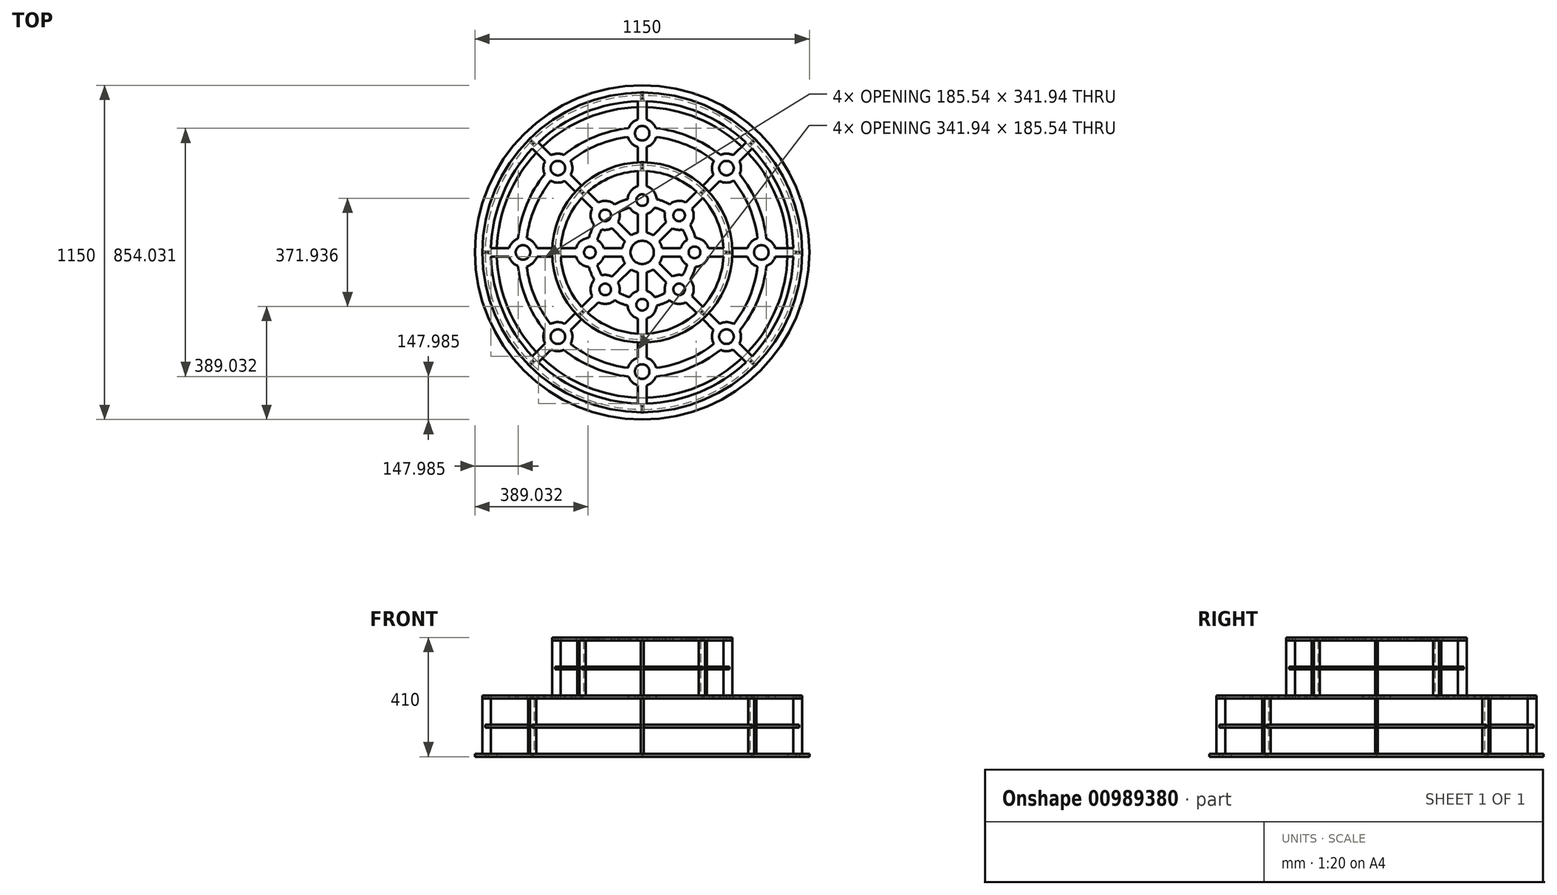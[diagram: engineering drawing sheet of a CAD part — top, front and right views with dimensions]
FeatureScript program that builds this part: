
annotation { "Feature Type Name" : "Feature", "Feature Type Description" : "" }
export const myFeature = defineFeature(function(context is Context, id is Id, definition is map)
    precondition{}
    {
        {
            var Q0;
            Q0=qCreatedBy(makeId("Top.planeOp"),FACE);
            cPlane(context, id + "F0", {"entities" : qUnion([Q0]), "cplaneType" : CPlaneType.OFFSET, "offset" : 200 * mm, "width" : 150 * mm, "height" : 150 * mm});
        }
        {
            var Q0;
            Q0=qCreatedBy(makeId("Top.planeOp"),FACE);
            cPlane(context, id + "F1", {"entities" : qUnion([Q0]), "cplaneType" : CPlaneType.OFFSET, "offset" : 200 * mm, "oppositeDirection" : true, "width" : 150 * mm, "height" : 150 * mm});
        }
        {
            var Q0;
            Q0=qCreatedBy(makeId("Top.planeOp"),FACE);
            cPlane(context, id + "F2", {"entities" : qUnion([Q0]), "cplaneType" : CPlaneType.OFFSET, "offset" : 100 * mm, "oppositeDirection" : true, "width" : 150 * mm, "height" : 150 * mm});
        }
        {
            var Q0;
            Q0=qCreatedBy(makeId("Top.planeOp"),FACE);
            cPlane(context, id + "F3", {"entities" : qUnion([Q0]), "cplaneType" : CPlaneType.OFFSET, "offset" : 100 * mm, "width" : 150 * mm, "height" : 150 * mm});
        }
        {
            var Q0;
            Q0=qCreatedBy(makeId("Top.planeOp"),FACE);
            var sketch = newSketch(context, id + "F4", { "sketchPlane" : qUnion([Q0])});
            skCircle(sketch, "E0", {"center": v(0, 0) * mm, "radius": 550 * mm});
            skArc(sketch, "E1", {"start": v(15, -519.78) * mm, "mid": v(199, -480.42) * mm, "end": v(356.94, -378.15) * mm});
            skArc(sketch, "E2", {"start": v(46.86, -427.44) * mm, "mid": v(164.55, -397.27) * mm, "end": v(269.1, -335.38) * mm});
            skArc(sketch, "E3", {"start": v(48.3, -397.07) * mm, "mid": v(153.07, -369.55) * mm, "end": v(246.62, -314.93) * mm});
            skArc(sketch, "E4", {"start": v(15, -309.64) * mm, "mid": v(118.63, -286.4) * mm, "end": v(208.34, -229.55) * mm});
            skCircle(sketch, "E5", {"center": v(0, 0) * mm, "radius": 280 * mm});
            skCircle(sketch, "E6", {"center": v(0, 0) * mm, "radius": 190 * mm, "construction": true});
            skCircle(sketch, "E7", {"center": v(0, 0) * mm, "radius": 160 * mm, "construction": true});
            skCircle(sketch, "E8", {"center": v(0, 0) * mm, "radius": 40 * mm, "construction": true});
            skCircle(sketch, "E9", {"center": v(0, 0) * mm, "radius": 70 * mm, "construction": true});
            skLineSegment(sketch, "E10", {"start": v(0, 725.48) * mm, "end": v(0, -722.46) * mm, "construction": true});
            skLineSegment(sketch, "E11", {"start": v(-695.44, 0) * mm, "end": v(901.66, 0) * mm, "construction": true});
            skArc(sketch, "E12", {"start": v(-15, -362.3) * mm, "mid": v(-36.11, -375.42) * mm, "end": v(-48.3, -397.07) * mm});
            skCircle(sketch, "E13", {"center": v(0, -410) * mm, "radius": 25 * mm});
            skLineSegment(sketch, "E14", {"start": v(15, -519.78) * mm, "end": v(15, -457.7) * mm});
            skLineSegment(sketch, "E15", {"start": v(-15, -457.7) * mm, "end": v(-15, -519.78) * mm});
            skLineSegment(sketch, "E16", {"start": v(-15, -362.3) * mm, "end": v(-15, -309.64) * mm});
            skLineSegment(sketch, "E17", {"start": v(15, -362.3) * mm, "end": v(15, -309.64) * mm});
            skArc(sketch, "E18.trimOffspring", {"start": v(-46.86, -427.44) * mm, "mid": v(-34.43, -446.26) * mm, "end": v(-15, -457.7) * mm});
            skArc(sketch, "E19.trimOffspring", {"start": v(48.3, -397.07) * mm, "mid": v(36.11, -375.42) * mm, "end": v(15, -362.3) * mm});
            skArc(sketch, "E20.trimOffspring", {"start": v(15, -457.7) * mm, "mid": v(34.43, -446.26) * mm, "end": v(46.86, -427.44) * mm});
            skArc(sketch, "E21.1.0", {"start": v(334.25, -313.03) * mm, "mid": v(339.9, -291.2) * mm, "end": v(335.38, -269.1) * mm});
            skCircle(sketch, "E21.1.1", {"center": v(289.91, -289.91) * mm, "radius": 25 * mm});
            skLineSegment(sketch, "E21.1.2", {"start": v(266.8, -245.58) * mm, "end": v(229.55, -208.34) * mm});
            skLineSegment(sketch, "E21.1.3", {"start": v(245.58, -266.8) * mm, "end": v(208.34, -229.55) * mm});
            skArc(sketch, "E21.1.4", {"start": v(245.58, -266.8) * mm, "mid": v(239.93, -291) * mm, "end": v(246.62, -314.93) * mm});
            skArc(sketch, "E21.1.5", {"start": v(269.1, -335.38) * mm, "mid": v(291.2, -339.9) * mm, "end": v(313.03, -334.25) * mm});
            skArc(sketch, "E21.1.6", {"start": v(314.93, -246.62) * mm, "mid": v(291, -239.93) * mm, "end": v(266.8, -245.58) * mm});
            skLineSegment(sketch, "E21.1.7", {"start": v(378.15, -356.94) * mm, "end": v(334.25, -313.03) * mm});
            skLineSegment(sketch, "E21.1.8", {"start": v(313.03, -334.25) * mm, "end": v(356.94, -378.15) * mm});
            skArc(sketch, "E21.2.0", {"start": v(457.7, 15) * mm, "mid": v(446.26, 34.43) * mm, "end": v(427.44, 46.86) * mm});
            skCircle(sketch, "E21.2.1", {"center": v(410, 0) * mm, "radius": 25 * mm});
            skLineSegment(sketch, "E21.2.2", {"start": v(362.3, 15) * mm, "end": v(309.64, 15) * mm});
            skLineSegment(sketch, "E21.2.3", {"start": v(362.3, -15) * mm, "end": v(309.64, -15) * mm});
            skArc(sketch, "E21.2.4", {"start": v(362.3, -15) * mm, "mid": v(375.42, -36.11) * mm, "end": v(397.07, -48.3) * mm});
            skArc(sketch, "E21.2.5", {"start": v(427.44, -46.86) * mm, "mid": v(446.26, -34.43) * mm, "end": v(457.7, -15) * mm});
            skArc(sketch, "E21.2.6", {"start": v(397.07, 48.3) * mm, "mid": v(375.42, 36.11) * mm, "end": v(362.3, 15) * mm});
            skLineSegment(sketch, "E21.2.7", {"start": v(519.78, 15) * mm, "end": v(457.7, 15) * mm});
            skLineSegment(sketch, "E21.2.8", {"start": v(457.7, -15) * mm, "end": v(519.78, -15) * mm});
            skArc(sketch, "E21.3.0", {"start": v(313.03, 334.25) * mm, "mid": v(291.2, 339.9) * mm, "end": v(269.1, 335.38) * mm});
            skCircle(sketch, "E21.3.1", {"center": v(289.91, 289.91) * mm, "radius": 25 * mm});
            skLineSegment(sketch, "E21.3.2", {"start": v(245.58, 266.8) * mm, "end": v(208.34, 229.55) * mm});
            skLineSegment(sketch, "E21.3.3", {"start": v(266.8, 245.58) * mm, "end": v(229.55, 208.34) * mm});
            skArc(sketch, "E21.3.4", {"start": v(266.8, 245.58) * mm, "mid": v(291, 239.93) * mm, "end": v(314.93, 246.62) * mm});
            skArc(sketch, "E21.3.5", {"start": v(335.38, 269.1) * mm, "mid": v(339.9, 291.2) * mm, "end": v(334.25, 313.03) * mm});
            skArc(sketch, "E21.3.6", {"start": v(246.62, 314.93) * mm, "mid": v(239.93, 291) * mm, "end": v(245.58, 266.8) * mm});
            skLineSegment(sketch, "E21.3.7", {"start": v(356.94, 378.15) * mm, "end": v(313.03, 334.25) * mm});
            skLineSegment(sketch, "E21.3.8", {"start": v(334.25, 313.03) * mm, "end": v(378.15, 356.94) * mm});
            skArc(sketch, "E21.4.0", {"start": v(-15, 457.7) * mm, "mid": v(-34.43, 446.26) * mm, "end": v(-46.86, 427.44) * mm});
            skCircle(sketch, "E21.4.1", {"center": v(0, 410) * mm, "radius": 25 * mm});
            skLineSegment(sketch, "E21.4.2", {"start": v(-15, 362.3) * mm, "end": v(-15, 309.64) * mm});
            skLineSegment(sketch, "E21.4.3", {"start": v(15, 362.3) * mm, "end": v(15, 309.64) * mm});
            skArc(sketch, "E21.4.4", {"start": v(15, 362.3) * mm, "mid": v(36.11, 375.42) * mm, "end": v(48.3, 397.07) * mm});
            skArc(sketch, "E21.4.5", {"start": v(46.86, 427.44) * mm, "mid": v(34.43, 446.26) * mm, "end": v(15, 457.7) * mm});
            skArc(sketch, "E21.4.6", {"start": v(-48.3, 397.07) * mm, "mid": v(-36.11, 375.42) * mm, "end": v(-15, 362.3) * mm});
            skLineSegment(sketch, "E21.4.7", {"start": v(-15, 519.78) * mm, "end": v(-15, 457.7) * mm});
            skLineSegment(sketch, "E21.4.8", {"start": v(15, 457.7) * mm, "end": v(15, 519.78) * mm});
            skArc(sketch, "E21.5.0", {"start": v(-334.25, 313.03) * mm, "mid": v(-339.9, 291.2) * mm, "end": v(-335.38, 269.1) * mm});
            skCircle(sketch, "E21.5.1", {"center": v(-289.91, 289.91) * mm, "radius": 25 * mm});
            skLineSegment(sketch, "E21.5.2", {"start": v(-266.8, 245.58) * mm, "end": v(-229.55, 208.34) * mm});
            skLineSegment(sketch, "E21.5.3", {"start": v(-245.58, 266.8) * mm, "end": v(-208.34, 229.55) * mm});
            skArc(sketch, "E21.5.4", {"start": v(-245.58, 266.8) * mm, "mid": v(-239.93, 291) * mm, "end": v(-246.62, 314.93) * mm});
            skArc(sketch, "E21.5.5", {"start": v(-269.1, 335.38) * mm, "mid": v(-291.2, 339.9) * mm, "end": v(-313.03, 334.25) * mm});
            skArc(sketch, "E21.5.6", {"start": v(-314.93, 246.62) * mm, "mid": v(-291, 239.93) * mm, "end": v(-266.8, 245.58) * mm});
            skLineSegment(sketch, "E21.5.7", {"start": v(-378.15, 356.94) * mm, "end": v(-334.25, 313.03) * mm});
            skLineSegment(sketch, "E21.5.8", {"start": v(-313.03, 334.25) * mm, "end": v(-356.94, 378.15) * mm});
            skArc(sketch, "E21.6.0", {"start": v(-457.7, -15) * mm, "mid": v(-446.26, -34.43) * mm, "end": v(-427.44, -46.86) * mm});
            skCircle(sketch, "E21.6.1", {"center": v(-410, 0) * mm, "radius": 25 * mm});
            skLineSegment(sketch, "E21.6.2", {"start": v(-362.3, -15) * mm, "end": v(-309.64, -15) * mm});
            skLineSegment(sketch, "E21.6.3", {"start": v(-362.3, 15) * mm, "end": v(-309.64, 15) * mm});
            skArc(sketch, "E21.6.4", {"start": v(-362.3, 15) * mm, "mid": v(-375.42, 36.11) * mm, "end": v(-397.07, 48.3) * mm});
            skArc(sketch, "E21.6.5", {"start": v(-427.44, 46.86) * mm, "mid": v(-446.26, 34.43) * mm, "end": v(-457.7, 15) * mm});
            skArc(sketch, "E21.6.6", {"start": v(-397.07, -48.3) * mm, "mid": v(-375.42, -36.11) * mm, "end": v(-362.3, -15) * mm});
            skLineSegment(sketch, "E21.6.7", {"start": v(-519.78, -15) * mm, "end": v(-457.7, -15) * mm});
            skLineSegment(sketch, "E21.6.8", {"start": v(-457.7, 15) * mm, "end": v(-519.78, 15) * mm});
            skArc(sketch, "E21.7.0", {"start": v(-313.03, -334.25) * mm, "mid": v(-291.2, -339.9) * mm, "end": v(-269.1, -335.38) * mm});
            skCircle(sketch, "E21.7.1", {"center": v(-289.91, -289.91) * mm, "radius": 25 * mm});
            skLineSegment(sketch, "E21.7.2", {"start": v(-245.58, -266.8) * mm, "end": v(-208.34, -229.55) * mm});
            skLineSegment(sketch, "E21.7.3", {"start": v(-266.8, -245.58) * mm, "end": v(-229.55, -208.34) * mm});
            skArc(sketch, "E21.7.4", {"start": v(-266.8, -245.58) * mm, "mid": v(-291, -239.93) * mm, "end": v(-314.93, -246.62) * mm});
            skArc(sketch, "E21.7.5", {"start": v(-335.38, -269.1) * mm, "mid": v(-339.9, -291.2) * mm, "end": v(-334.25, -313.03) * mm});
            skArc(sketch, "E21.7.6", {"start": v(-246.62, -314.93) * mm, "mid": v(-239.93, -291) * mm, "end": v(-245.58, -266.8) * mm});
            skLineSegment(sketch, "E21.7.7", {"start": v(-356.94, -378.15) * mm, "end": v(-313.03, -334.25) * mm});
            skLineSegment(sketch, "E21.7.8", {"start": v(-334.25, -313.03) * mm, "end": v(-378.15, -356.94) * mm});
            skArc(sketch, "E22.trimOffspring", {"start": v(-246.62, -314.93) * mm, "mid": v(-153.07, -369.55) * mm, "end": v(-48.3, -397.07) * mm});
            skArc(sketch, "E23.trimOffspring", {"start": v(-269.1, -335.38) * mm, "mid": v(-164.55, -397.27) * mm, "end": v(-46.86, -427.44) * mm});
            skArc(sketch, "E24.trimOffspring", {"start": v(-356.94, -378.15) * mm, "mid": v(-199, -480.42) * mm, "end": v(-15, -519.78) * mm});
            skArc(sketch, "E25.trimOffspring", {"start": v(-208.34, -229.55) * mm, "mid": v(-118.63, -286.4) * mm, "end": v(-15, -309.64) * mm});
            skArc(sketch, "E26.trimOffspring", {"start": v(-397.07, -48.3) * mm, "mid": v(-369.55, -153.07) * mm, "end": v(-314.93, -246.62) * mm});
            skArc(sketch, "E27.trimOffspring", {"start": v(-427.44, -46.86) * mm, "mid": v(-397.27, -164.55) * mm, "end": v(-335.38, -269.1) * mm});
            skArc(sketch, "E28.trimOffspring", {"start": v(-309.64, -15) * mm, "mid": v(-286.4, -118.63) * mm, "end": v(-229.55, -208.34) * mm});
            skArc(sketch, "E29.trimOffspring", {"start": v(-519.78, -15) * mm, "mid": v(-480.42, -199) * mm, "end": v(-378.15, -356.94) * mm});
            skArc(sketch, "E30.trimOffspring", {"start": v(-314.93, 246.62) * mm, "mid": v(-369.55, 153.07) * mm, "end": v(-397.07, 48.3) * mm});
            skArc(sketch, "E31.trimOffspring", {"start": v(-335.38, 269.1) * mm, "mid": v(-397.27, 164.55) * mm, "end": v(-427.44, 46.86) * mm});
            skArc(sketch, "E32.trimOffspring", {"start": v(-378.15, 356.94) * mm, "mid": v(-480.42, 199) * mm, "end": v(-519.78, 15) * mm});
            skArc(sketch, "E33.trimOffspring", {"start": v(-229.55, 208.34) * mm, "mid": v(-286.4, 118.63) * mm, "end": v(-309.64, 15) * mm});
            skArc(sketch, "E34.trimOffspring", {"start": v(-15, 309.64) * mm, "mid": v(-118.63, 286.4) * mm, "end": v(-208.34, 229.55) * mm});
            skArc(sketch, "E35.trimOffspring", {"start": v(-48.3, 397.07) * mm, "mid": v(-153.07, 369.55) * mm, "end": v(-246.62, 314.93) * mm});
            skArc(sketch, "E36.trimOffspring", {"start": v(-46.86, 427.44) * mm, "mid": v(-164.55, 397.27) * mm, "end": v(-269.1, 335.38) * mm});
            skArc(sketch, "E37.trimOffspring", {"start": v(-15, 519.78) * mm, "mid": v(-199, 480.42) * mm, "end": v(-356.94, 378.15) * mm});
            skArc(sketch, "E38.trimOffspring", {"start": v(269.1, 335.38) * mm, "mid": v(164.55, 397.27) * mm, "end": v(46.86, 427.44) * mm});
            skArc(sketch, "E39.trimOffspring", {"start": v(246.62, 314.93) * mm, "mid": v(153.07, 369.55) * mm, "end": v(48.3, 397.07) * mm});
            skArc(sketch, "E40.trimOffspring", {"start": v(208.34, 229.55) * mm, "mid": v(118.63, 286.4) * mm, "end": v(15, 309.64) * mm});
            skArc(sketch, "E41.trimOffspring", {"start": v(356.94, 378.15) * mm, "mid": v(199, 480.42) * mm, "end": v(15, 519.78) * mm});
            skArc(sketch, "E42.trimOffspring", {"start": v(309.64, 15) * mm, "mid": v(286.4, 118.63) * mm, "end": v(229.55, 208.34) * mm});
            skArc(sketch, "E43.trimOffspring", {"start": v(397.07, 48.3) * mm, "mid": v(369.55, 153.07) * mm, "end": v(314.93, 246.62) * mm});
            skArc(sketch, "E44.trimOffspring", {"start": v(427.44, 46.86) * mm, "mid": v(397.27, 164.55) * mm, "end": v(335.38, 269.1) * mm});
            skArc(sketch, "E45.trimOffspring", {"start": v(519.78, 15) * mm, "mid": v(480.42, 199) * mm, "end": v(378.15, 356.94) * mm});
            skArc(sketch, "E46.trimOffspring", {"start": v(335.38, -269.1) * mm, "mid": v(397.27, -164.55) * mm, "end": v(427.44, -46.86) * mm});
            skArc(sketch, "E47.trimOffspring", {"start": v(314.93, -246.62) * mm, "mid": v(369.55, -153.07) * mm, "end": v(397.07, -48.3) * mm});
            skArc(sketch, "E48.trimOffspring", {"start": v(378.15, -356.94) * mm, "mid": v(480.42, -199) * mm, "end": v(519.78, -15) * mm});
            skArc(sketch, "E49.trimOffspring", {"start": v(229.55, -208.34) * mm, "mid": v(286.4, -118.63) * mm, "end": v(309.64, -15) * mm});
            skLineSegment(sketch, "E50.bottom", {"start": v(4.9, 530) * mm, "end": v(1, 530) * mm});
            skLineSegment(sketch, "E50.top", {"start": v(4.9, 540) * mm, "end": v(1, 540) * mm});
            skLineSegment(sketch, "E50.left", {"start": v(4.9, 530) * mm, "end": v(4.9, 540) * mm});
            skLineSegment(sketch, "E50.right", {"start": v(-4.9, 530) * mm, "end": v(-4.9, 540) * mm});
            skPoint(sketch, "E50.middle", {"position": v(0, 535) * mm});
            skLineSegment(sketch, "E51", {"start": v(0, 541) * mm, "end": v(-1, 540) * mm});
            skLineSegment(sketch, "E52", {"start": v(0, 541) * mm, "end": v(1, 540) * mm});
            skLineSegment(sketch, "E53.trimOffspring", {"start": v(-1, 540) * mm, "end": v(-4.9, 540) * mm});
            skLineSegment(sketch, "E54", {"start": v(0, 529) * mm, "end": v(-1, 530) * mm});
            skLineSegment(sketch, "E55", {"start": v(0, 529) * mm, "end": v(1, 530) * mm});
            skLineSegment(sketch, "E56.trimOffspring", {"start": v(-1, 530) * mm, "end": v(-4.9, 530) * mm});
            skPoint(sketch, "E57.1.0", {"position": v(-378.3, 378.3) * mm});
            skLineSegment(sketch, "E57.1.1", {"start": v(-378.23, 371.3) * mm, "end": v(-385.3, 378.37) * mm});
            skLineSegment(sketch, "E57.1.2", {"start": v(-371.3, 378.23) * mm, "end": v(-378.37, 385.3) * mm});
            skLineSegment(sketch, "E57.1.3", {"start": v(-371.3, 378.23) * mm, "end": v(-374.06, 375.47) * mm});
            skLineSegment(sketch, "E57.1.4", {"start": v(-374.06, 374.06) * mm, "end": v(-374.06, 375.47) * mm});
            skLineSegment(sketch, "E57.1.5", {"start": v(-374.06, 374.06) * mm, "end": v(-375.47, 374.06) * mm});
            skLineSegment(sketch, "E57.1.6", {"start": v(-375.47, 374.06) * mm, "end": v(-378.23, 371.3) * mm});
            skLineSegment(sketch, "E57.1.7", {"start": v(-378.37, 385.3) * mm, "end": v(-381.13, 382.54) * mm});
            skLineSegment(sketch, "E57.1.8", {"start": v(-382.54, 381.13) * mm, "end": v(-385.3, 378.37) * mm});
            skLineSegment(sketch, "E57.1.9", {"start": v(-382.54, 382.54) * mm, "end": v(-381.13, 382.54) * mm});
            skLineSegment(sketch, "E57.1.10", {"start": v(-382.54, 382.54) * mm, "end": v(-382.54, 381.13) * mm});
            skPoint(sketch, "E57.2.0", {"position": v(-535, 0) * mm});
            skLineSegment(sketch, "E57.2.1", {"start": v(-530, -4.9) * mm, "end": v(-540, -4.9) * mm});
            skLineSegment(sketch, "E57.2.2", {"start": v(-530, 4.9) * mm, "end": v(-540, 4.9) * mm});
            skLineSegment(sketch, "E57.2.3", {"start": v(-530, 4.9) * mm, "end": v(-530, 1) * mm});
            skLineSegment(sketch, "E57.2.4", {"start": v(-529, 0) * mm, "end": v(-530, 1) * mm});
            skLineSegment(sketch, "E57.2.5", {"start": v(-529, 0) * mm, "end": v(-530, -1) * mm});
            skLineSegment(sketch, "E57.2.6", {"start": v(-530, -1) * mm, "end": v(-530, -4.9) * mm});
            skLineSegment(sketch, "E57.2.7", {"start": v(-540, 4.9) * mm, "end": v(-540, 1) * mm});
            skLineSegment(sketch, "E57.2.8", {"start": v(-540, -1) * mm, "end": v(-540, -4.9) * mm});
            skLineSegment(sketch, "E57.2.9", {"start": v(-541, 0) * mm, "end": v(-540, 1) * mm});
            skLineSegment(sketch, "E57.2.10", {"start": v(-541, 0) * mm, "end": v(-540, -1) * mm});
            skPoint(sketch, "E57.3.0", {"position": v(-378.3, -378.3) * mm});
            skLineSegment(sketch, "E57.3.1", {"start": v(-371.3, -378.23) * mm, "end": v(-378.37, -385.3) * mm});
            skLineSegment(sketch, "E57.3.2", {"start": v(-378.23, -371.3) * mm, "end": v(-385.3, -378.37) * mm});
            skLineSegment(sketch, "E57.3.3", {"start": v(-378.23, -371.3) * mm, "end": v(-375.47, -374.06) * mm});
            skLineSegment(sketch, "E57.3.4", {"start": v(-374.06, -374.06) * mm, "end": v(-375.47, -374.06) * mm});
            skLineSegment(sketch, "E57.3.5", {"start": v(-374.06, -374.06) * mm, "end": v(-374.06, -375.47) * mm});
            skLineSegment(sketch, "E57.3.6", {"start": v(-374.06, -375.47) * mm, "end": v(-371.3, -378.23) * mm});
            skLineSegment(sketch, "E57.3.7", {"start": v(-385.3, -378.37) * mm, "end": v(-382.54, -381.13) * mm});
            skLineSegment(sketch, "E57.3.8", {"start": v(-381.13, -382.54) * mm, "end": v(-378.37, -385.3) * mm});
            skLineSegment(sketch, "E57.3.9", {"start": v(-382.54, -382.54) * mm, "end": v(-382.54, -381.13) * mm});
            skLineSegment(sketch, "E57.3.10", {"start": v(-382.54, -382.54) * mm, "end": v(-381.13, -382.54) * mm});
            skPoint(sketch, "E57.4.0", {"position": v(0, -535) * mm});
            skLineSegment(sketch, "E57.4.1", {"start": v(4.9, -530) * mm, "end": v(4.9, -540) * mm});
            skLineSegment(sketch, "E57.4.2", {"start": v(-4.9, -530) * mm, "end": v(-4.9, -540) * mm});
            skLineSegment(sketch, "E57.4.3", {"start": v(-4.9, -530) * mm, "end": v(-1, -530) * mm});
            skLineSegment(sketch, "E57.4.4", {"start": v(0, -529) * mm, "end": v(-1, -530) * mm});
            skLineSegment(sketch, "E57.4.5", {"start": v(0, -529) * mm, "end": v(1, -530) * mm});
            skLineSegment(sketch, "E57.4.6", {"start": v(1, -530) * mm, "end": v(4.9, -530) * mm});
            skLineSegment(sketch, "E57.4.7", {"start": v(-4.9, -540) * mm, "end": v(-1, -540) * mm});
            skLineSegment(sketch, "E57.4.8", {"start": v(1, -540) * mm, "end": v(4.9, -540) * mm});
            skLineSegment(sketch, "E57.4.9", {"start": v(0, -541) * mm, "end": v(-1, -540) * mm});
            skLineSegment(sketch, "E57.4.10", {"start": v(0, -541) * mm, "end": v(1, -540) * mm});
            skPoint(sketch, "E57.5.0", {"position": v(378.3, -378.3) * mm});
            skLineSegment(sketch, "E57.5.1", {"start": v(378.23, -371.3) * mm, "end": v(385.3, -378.37) * mm});
            skLineSegment(sketch, "E57.5.2", {"start": v(371.3, -378.23) * mm, "end": v(378.37, -385.3) * mm});
            skLineSegment(sketch, "E57.5.3", {"start": v(371.3, -378.23) * mm, "end": v(374.06, -375.47) * mm});
            skLineSegment(sketch, "E57.5.4", {"start": v(374.06, -374.06) * mm, "end": v(374.06, -375.47) * mm});
            skLineSegment(sketch, "E57.5.5", {"start": v(374.06, -374.06) * mm, "end": v(375.47, -374.06) * mm});
            skLineSegment(sketch, "E57.5.6", {"start": v(375.47, -374.06) * mm, "end": v(378.23, -371.3) * mm});
            skLineSegment(sketch, "E57.5.7", {"start": v(378.37, -385.3) * mm, "end": v(381.13, -382.54) * mm});
            skLineSegment(sketch, "E57.5.8", {"start": v(382.54, -381.13) * mm, "end": v(385.3, -378.37) * mm});
            skLineSegment(sketch, "E57.5.9", {"start": v(382.54, -382.54) * mm, "end": v(381.13, -382.54) * mm});
            skLineSegment(sketch, "E57.5.10", {"start": v(382.54, -382.54) * mm, "end": v(382.54, -381.13) * mm});
            skPoint(sketch, "E57.6.0", {"position": v(535, 0) * mm});
            skLineSegment(sketch, "E57.6.1", {"start": v(530, 4.9) * mm, "end": v(540, 4.9) * mm});
            skLineSegment(sketch, "E57.6.2", {"start": v(530, -4.9) * mm, "end": v(540, -4.9) * mm});
            skLineSegment(sketch, "E57.6.3", {"start": v(530, -4.9) * mm, "end": v(530, -1) * mm});
            skLineSegment(sketch, "E57.6.4", {"start": v(529, 0) * mm, "end": v(530, -1) * mm});
            skLineSegment(sketch, "E57.6.5", {"start": v(529, 0) * mm, "end": v(530, 1) * mm});
            skLineSegment(sketch, "E57.6.6", {"start": v(530, 1) * mm, "end": v(530, 4.9) * mm});
            skLineSegment(sketch, "E57.6.7", {"start": v(540, -4.9) * mm, "end": v(540, -1) * mm});
            skLineSegment(sketch, "E57.6.8", {"start": v(540, 1) * mm, "end": v(540, 4.9) * mm});
            skLineSegment(sketch, "E57.6.9", {"start": v(541, 0) * mm, "end": v(540, -1) * mm});
            skLineSegment(sketch, "E57.6.10", {"start": v(541, 0) * mm, "end": v(540, 1) * mm});
            skPoint(sketch, "E57.7.0", {"position": v(378.3, 378.3) * mm});
            skLineSegment(sketch, "E57.7.1", {"start": v(371.3, 378.23) * mm, "end": v(378.37, 385.3) * mm});
            skLineSegment(sketch, "E57.7.2", {"start": v(378.23, 371.3) * mm, "end": v(385.3, 378.37) * mm});
            skLineSegment(sketch, "E57.7.3", {"start": v(378.23, 371.3) * mm, "end": v(375.47, 374.06) * mm});
            skLineSegment(sketch, "E57.7.4", {"start": v(374.06, 374.06) * mm, "end": v(375.47, 374.06) * mm});
            skLineSegment(sketch, "E57.7.5", {"start": v(374.06, 374.06) * mm, "end": v(374.06, 375.47) * mm});
            skLineSegment(sketch, "E57.7.6", {"start": v(374.06, 375.47) * mm, "end": v(371.3, 378.23) * mm});
            skLineSegment(sketch, "E57.7.7", {"start": v(385.3, 378.37) * mm, "end": v(382.54, 381.13) * mm});
            skLineSegment(sketch, "E57.7.8", {"start": v(381.13, 382.54) * mm, "end": v(378.37, 385.3) * mm});
            skLineSegment(sketch, "E57.7.9", {"start": v(382.54, 382.54) * mm, "end": v(382.54, 381.13) * mm});
            skLineSegment(sketch, "E57.7.10", {"start": v(382.54, 382.54) * mm, "end": v(381.13, 382.54) * mm});
            skLineSegment(sketch, "E58.bottom", {"start": v(4.9, 290) * mm, "end": v(1, 290) * mm});
            skLineSegment(sketch, "E58.top", {"start": v(4.9, 300) * mm, "end": v(1, 300) * mm});
            skLineSegment(sketch, "E58.left", {"start": v(4.9, 290) * mm, "end": v(4.9, 300) * mm});
            skLineSegment(sketch, "E58.right", {"start": v(-4.9, 290) * mm, "end": v(-4.9, 300) * mm});
            skPoint(sketch, "E58.middle", {"position": v(0, 295) * mm});
            skLineSegment(sketch, "E59", {"start": v(0, 301) * mm, "end": v(-1, 300) * mm});
            skLineSegment(sketch, "E60", {"start": v(0, 301) * mm, "end": v(1, 300) * mm});
            skLineSegment(sketch, "E61.trimOffspring", {"start": v(-1, 300) * mm, "end": v(-4.9, 300) * mm});
            skLineSegment(sketch, "E62", {"start": v(0, 289) * mm, "end": v(-1, 290) * mm});
            skLineSegment(sketch, "E63", {"start": v(0, 289) * mm, "end": v(1, 290) * mm});
            skLineSegment(sketch, "E64.trimOffspring", {"start": v(-1, 290) * mm, "end": v(-4.9, 290) * mm});
            skLineSegment(sketch, "E65.1.0", {"start": v(-201.6, 208.53) * mm, "end": v(-208.67, 215.6) * mm});
            skPoint(sketch, "E65.1.1", {"position": v(-208.6, 208.6) * mm});
            skLineSegment(sketch, "E65.1.2", {"start": v(-208.53, 201.6) * mm, "end": v(-215.6, 208.67) * mm});
            skLineSegment(sketch, "E65.1.3", {"start": v(-205.77, 204.35) * mm, "end": v(-208.53, 201.6) * mm});
            skLineSegment(sketch, "E65.1.4", {"start": v(-208.67, 215.6) * mm, "end": v(-211.42, 212.84) * mm});
            skLineSegment(sketch, "E65.1.5", {"start": v(-201.6, 208.53) * mm, "end": v(-204.35, 205.77) * mm});
            skLineSegment(sketch, "E65.1.6", {"start": v(-212.84, 211.42) * mm, "end": v(-215.6, 208.67) * mm});
            skLineSegment(sketch, "E65.1.7", {"start": v(-204.35, 204.35) * mm, "end": v(-205.77, 204.35) * mm});
            skLineSegment(sketch, "E65.1.8", {"start": v(-212.84, 212.84) * mm, "end": v(-211.42, 212.84) * mm});
            skLineSegment(sketch, "E65.1.9", {"start": v(-212.84, 212.84) * mm, "end": v(-212.84, 211.42) * mm});
            skLineSegment(sketch, "E65.1.10", {"start": v(-204.35, 204.35) * mm, "end": v(-204.35, 205.77) * mm});
            skLineSegment(sketch, "E65.2.0", {"start": v(-290, 4.9) * mm, "end": v(-300, 4.9) * mm});
            skPoint(sketch, "E65.2.1", {"position": v(-295, 0) * mm});
            skLineSegment(sketch, "E65.2.2", {"start": v(-290, -4.9) * mm, "end": v(-300, -4.9) * mm});
            skLineSegment(sketch, "E65.2.3", {"start": v(-290, -1) * mm, "end": v(-290, -4.9) * mm});
            skLineSegment(sketch, "E65.2.4", {"start": v(-300, 4.9) * mm, "end": v(-300, 1) * mm});
            skLineSegment(sketch, "E65.2.5", {"start": v(-290, 4.9) * mm, "end": v(-290, 1) * mm});
            skLineSegment(sketch, "E65.2.6", {"start": v(-300, -1) * mm, "end": v(-300, -4.9) * mm});
            skLineSegment(sketch, "E65.2.7", {"start": v(-289, 0) * mm, "end": v(-290, -1) * mm});
            skLineSegment(sketch, "E65.2.8", {"start": v(-301, 0) * mm, "end": v(-300, 1) * mm});
            skLineSegment(sketch, "E65.2.9", {"start": v(-301, 0) * mm, "end": v(-300, -1) * mm});
            skLineSegment(sketch, "E65.2.10", {"start": v(-289, 0) * mm, "end": v(-290, 1) * mm});
            skLineSegment(sketch, "E65.3.0", {"start": v(-208.53, -201.6) * mm, "end": v(-215.6, -208.67) * mm});
            skPoint(sketch, "E65.3.1", {"position": v(-208.6, -208.6) * mm});
            skLineSegment(sketch, "E65.3.2", {"start": v(-201.6, -208.53) * mm, "end": v(-208.67, -215.6) * mm});
            skLineSegment(sketch, "E65.3.3", {"start": v(-204.35, -205.77) * mm, "end": v(-201.6, -208.53) * mm});
            skLineSegment(sketch, "E65.3.4", {"start": v(-215.6, -208.67) * mm, "end": v(-212.84, -211.42) * mm});
            skLineSegment(sketch, "E65.3.5", {"start": v(-208.53, -201.6) * mm, "end": v(-205.77, -204.35) * mm});
            skLineSegment(sketch, "E65.3.6", {"start": v(-211.42, -212.84) * mm, "end": v(-208.67, -215.6) * mm});
            skLineSegment(sketch, "E65.3.7", {"start": v(-204.35, -204.35) * mm, "end": v(-204.35, -205.77) * mm});
            skLineSegment(sketch, "E65.3.8", {"start": v(-212.84, -212.84) * mm, "end": v(-212.84, -211.42) * mm});
            skLineSegment(sketch, "E65.3.9", {"start": v(-212.84, -212.84) * mm, "end": v(-211.42, -212.84) * mm});
            skLineSegment(sketch, "E65.3.10", {"start": v(-204.35, -204.35) * mm, "end": v(-205.77, -204.35) * mm});
            skLineSegment(sketch, "E65.4.0", {"start": v(-4.9, -290) * mm, "end": v(-4.9, -300) * mm});
            skPoint(sketch, "E65.4.1", {"position": v(0, -295) * mm});
            skLineSegment(sketch, "E65.4.2", {"start": v(4.9, -290) * mm, "end": v(4.9, -300) * mm});
            skLineSegment(sketch, "E65.4.3", {"start": v(1, -290) * mm, "end": v(4.9, -290) * mm});
            skLineSegment(sketch, "E65.4.4", {"start": v(-4.9, -300) * mm, "end": v(-1, -300) * mm});
            skLineSegment(sketch, "E65.4.5", {"start": v(-4.9, -290) * mm, "end": v(-1, -290) * mm});
            skLineSegment(sketch, "E65.4.6", {"start": v(1, -300) * mm, "end": v(4.9, -300) * mm});
            skLineSegment(sketch, "E65.4.7", {"start": v(0, -289) * mm, "end": v(1, -290) * mm});
            skLineSegment(sketch, "E65.4.8", {"start": v(0, -301) * mm, "end": v(-1, -300) * mm});
            skLineSegment(sketch, "E65.4.9", {"start": v(0, -301) * mm, "end": v(1, -300) * mm});
            skLineSegment(sketch, "E65.4.10", {"start": v(0, -289) * mm, "end": v(-1, -290) * mm});
            skLineSegment(sketch, "E65.5.0", {"start": v(201.6, -208.53) * mm, "end": v(208.67, -215.6) * mm});
            skPoint(sketch, "E65.5.1", {"position": v(208.6, -208.6) * mm});
            skLineSegment(sketch, "E65.5.2", {"start": v(208.53, -201.6) * mm, "end": v(215.6, -208.67) * mm});
            skLineSegment(sketch, "E65.5.3", {"start": v(205.77, -204.35) * mm, "end": v(208.53, -201.6) * mm});
            skLineSegment(sketch, "E65.5.4", {"start": v(208.67, -215.6) * mm, "end": v(211.42, -212.84) * mm});
            skLineSegment(sketch, "E65.5.5", {"start": v(201.6, -208.53) * mm, "end": v(204.35, -205.77) * mm});
            skLineSegment(sketch, "E65.5.6", {"start": v(212.84, -211.42) * mm, "end": v(215.6, -208.67) * mm});
            skLineSegment(sketch, "E65.5.7", {"start": v(204.35, -204.35) * mm, "end": v(205.77, -204.35) * mm});
            skLineSegment(sketch, "E65.5.8", {"start": v(212.84, -212.84) * mm, "end": v(211.42, -212.84) * mm});
            skLineSegment(sketch, "E65.5.9", {"start": v(212.84, -212.84) * mm, "end": v(212.84, -211.42) * mm});
            skLineSegment(sketch, "E65.5.10", {"start": v(204.35, -204.35) * mm, "end": v(204.35, -205.77) * mm});
            skLineSegment(sketch, "E65.6.0", {"start": v(290, -4.9) * mm, "end": v(300, -4.9) * mm});
            skPoint(sketch, "E65.6.1", {"position": v(295, 0) * mm});
            skLineSegment(sketch, "E65.6.2", {"start": v(290, 4.9) * mm, "end": v(300, 4.9) * mm});
            skLineSegment(sketch, "E65.6.3", {"start": v(290, 1) * mm, "end": v(290, 4.9) * mm});
            skLineSegment(sketch, "E65.6.4", {"start": v(300, -4.9) * mm, "end": v(300, -1) * mm});
            skLineSegment(sketch, "E65.6.5", {"start": v(290, -4.9) * mm, "end": v(290, -1) * mm});
            skLineSegment(sketch, "E65.6.6", {"start": v(300, 1) * mm, "end": v(300, 4.9) * mm});
            skLineSegment(sketch, "E65.6.7", {"start": v(289, 0) * mm, "end": v(290, 1) * mm});
            skLineSegment(sketch, "E65.6.8", {"start": v(301, 0) * mm, "end": v(300, -1) * mm});
            skLineSegment(sketch, "E65.6.9", {"start": v(301, 0) * mm, "end": v(300, 1) * mm});
            skLineSegment(sketch, "E65.6.10", {"start": v(289, 0) * mm, "end": v(290, -1) * mm});
            skLineSegment(sketch, "E65.7.0", {"start": v(208.53, 201.6) * mm, "end": v(215.6, 208.67) * mm});
            skPoint(sketch, "E65.7.1", {"position": v(208.6, 208.6) * mm});
            skLineSegment(sketch, "E65.7.2", {"start": v(201.6, 208.53) * mm, "end": v(208.67, 215.6) * mm});
            skLineSegment(sketch, "E65.7.3", {"start": v(204.35, 205.77) * mm, "end": v(201.6, 208.53) * mm});
            skLineSegment(sketch, "E65.7.4", {"start": v(215.6, 208.67) * mm, "end": v(212.84, 211.42) * mm});
            skLineSegment(sketch, "E65.7.5", {"start": v(208.53, 201.6) * mm, "end": v(205.77, 204.35) * mm});
            skLineSegment(sketch, "E65.7.6", {"start": v(211.42, 212.84) * mm, "end": v(208.67, 215.6) * mm});
            skLineSegment(sketch, "E65.7.7", {"start": v(204.35, 204.35) * mm, "end": v(204.35, 205.77) * mm});
            skLineSegment(sketch, "E65.7.8", {"start": v(212.84, 212.84) * mm, "end": v(212.84, 211.42) * mm});
            skLineSegment(sketch, "E65.7.9", {"start": v(212.84, 212.84) * mm, "end": v(211.42, 212.84) * mm});
            skLineSegment(sketch, "E65.7.10", {"start": v(204.35, 204.35) * mm, "end": v(205.77, 204.35) * mm});
            skSolve(sketch);
        }
        {
            var Q0;
            Q0=qSketchRegion(id+"F4",true);
            extrude(context, id + "F5", {"entities" : qUnion([Q0]), "depth" : 10 * mm, "offsetDistance" : 25 * mm});
        }
        {
            var Q0;
            Q0=qCreatedBy(id+"F0.planeOp",FACE);
            var sketch = newSketch(context, id + "F6", { "sketchPlane" : qUnion([Q0])});
            skArc(sketch, "E66.0", {"start": v(42.8, -154.17) * mm, "mid": v(61.23, -147.82) * mm, "end": v(78.74, -139.28) * mm});
            skArc(sketch, "E67.0", {"start": v(49.89, -183.33) * mm, "mid": v(72.7, -175.54) * mm, "end": v(94.36, -164.91) * mm});
            skArc(sketch, "E68.0", {"start": v(15, -279.6) * mm, "mid": v(107.15, -258.69) * mm, "end": v(187.1, -208.31) * mm});
            skArc(sketch, "E69.0", {"start": v(15, -68.37) * mm, "mid": v(26.79, -64.67) * mm, "end": v(37.74, -58.95) * mm});
            skCircle(sketch, "E70.0", {"center": v(0, 0) * mm, "radius": 40 * mm});
            skPoint(sketch, "E71.0", {"position": v(15, 309.64) * mm});
            skCircle(sketch, "E72", {"center": v(0, 0) * mm, "radius": 310 * mm});
            skArc(sketch, "E73", {"start": v(-15, -132.3) * mm, "mid": v(-30.9, -140.7) * mm, "end": v(-42.8, -154.17) * mm});
            skCircle(sketch, "E74", {"center": v(0, -180) * mm, "radius": 20 * mm});
            skLineSegment(sketch, "E75", {"start": v(-15, -68.37) * mm, "end": v(-15, -132.3) * mm});
            skLineSegment(sketch, "E76", {"start": v(15, -68.37) * mm, "end": v(15, -132.3) * mm});
            skLineSegment(sketch, "E77", {"start": v(-15, -227.7) * mm, "end": v(-15, -279.6) * mm});
            skLineSegment(sketch, "E78", {"start": v(15, -227.7) * mm, "end": v(15, -279.6) * mm});
            skArc(sketch, "E79.trimOffspring", {"start": v(42.8, -154.17) * mm, "mid": v(30.9, -140.7) * mm, "end": v(15, -132.3) * mm});
            skArc(sketch, "E80.trimOffspring", {"start": v(15, -227.7) * mm, "mid": v(39.3, -210.9) * mm, "end": v(49.89, -183.33) * mm});
            skArc(sketch, "E81.trimOffspring", {"start": v(-49.89, -183.33) * mm, "mid": v(-39.3, -210.9) * mm, "end": v(-15, -227.7) * mm});
            skLineSegment(sketch, "E82.1.0", {"start": v(58.95, -37.74) * mm, "end": v(104.16, -82.95) * mm});
            skLineSegment(sketch, "E82.1.1", {"start": v(37.74, -58.95) * mm, "end": v(82.95, -104.16) * mm});
            skArc(sketch, "E82.1.2", {"start": v(82.95, -104.16) * mm, "mid": v(77.63, -121.34) * mm, "end": v(78.74, -139.28) * mm});
            skCircle(sketch, "E82.1.3", {"center": v(127.28, -127.28) * mm, "radius": 20 * mm});
            skArc(sketch, "E82.1.4", {"start": v(94.36, -164.91) * mm, "mid": v(121.34, -176.93) * mm, "end": v(150.4, -171.61) * mm});
            skArc(sketch, "E82.1.5", {"start": v(171.61, -150.4) * mm, "mid": v(176.93, -121.34) * mm, "end": v(164.91, -94.36) * mm});
            skArc(sketch, "E82.1.6", {"start": v(139.28, -78.74) * mm, "mid": v(121.34, -77.63) * mm, "end": v(104.16, -82.95) * mm});
            skLineSegment(sketch, "E82.1.7", {"start": v(171.61, -150.4) * mm, "end": v(208.31, -187.1) * mm});
            skLineSegment(sketch, "E82.1.8", {"start": v(150.4, -171.61) * mm, "end": v(187.1, -208.31) * mm});
            skLineSegment(sketch, "E82.2.0", {"start": v(68.37, 15) * mm, "end": v(132.3, 15) * mm});
            skLineSegment(sketch, "E82.2.1", {"start": v(68.37, -15) * mm, "end": v(132.3, -15) * mm});
            skArc(sketch, "E82.2.2", {"start": v(132.3, -15) * mm, "mid": v(140.7, -30.9) * mm, "end": v(154.17, -42.8) * mm});
            skCircle(sketch, "E82.2.3", {"center": v(180, 0) * mm, "radius": 20 * mm});
            skArc(sketch, "E82.2.4", {"start": v(183.33, -49.89) * mm, "mid": v(210.9, -39.3) * mm, "end": v(227.7, -15) * mm});
            skArc(sketch, "E82.2.5", {"start": v(227.7, 15) * mm, "mid": v(210.9, 39.3) * mm, "end": v(183.33, 49.89) * mm});
            skArc(sketch, "E82.2.6", {"start": v(154.17, 42.8) * mm, "mid": v(140.7, 30.9) * mm, "end": v(132.3, 15) * mm});
            skLineSegment(sketch, "E82.2.7", {"start": v(227.7, 15) * mm, "end": v(279.6, 15) * mm});
            skLineSegment(sketch, "E82.2.8", {"start": v(227.7, -15) * mm, "end": v(279.6, -15) * mm});
            skLineSegment(sketch, "E82.3.0", {"start": v(37.74, 58.95) * mm, "end": v(82.95, 104.16) * mm});
            skLineSegment(sketch, "E82.3.1", {"start": v(58.95, 37.74) * mm, "end": v(104.16, 82.95) * mm});
            skArc(sketch, "E82.3.2", {"start": v(104.16, 82.95) * mm, "mid": v(121.34, 77.63) * mm, "end": v(139.28, 78.74) * mm});
            skCircle(sketch, "E82.3.3", {"center": v(127.28, 127.28) * mm, "radius": 20 * mm});
            skArc(sketch, "E82.3.4", {"start": v(164.91, 94.36) * mm, "mid": v(176.93, 121.34) * mm, "end": v(171.61, 150.4) * mm});
            skArc(sketch, "E82.3.5", {"start": v(150.4, 171.61) * mm, "mid": v(121.34, 176.93) * mm, "end": v(94.36, 164.91) * mm});
            skArc(sketch, "E82.3.6", {"start": v(78.74, 139.28) * mm, "mid": v(77.63, 121.34) * mm, "end": v(82.95, 104.16) * mm});
            skLineSegment(sketch, "E82.3.7", {"start": v(150.4, 171.61) * mm, "end": v(187.1, 208.31) * mm});
            skLineSegment(sketch, "E82.3.8", {"start": v(171.61, 150.4) * mm, "end": v(208.31, 187.1) * mm});
            skLineSegment(sketch, "E82.4.0", {"start": v(-15, 68.37) * mm, "end": v(-15, 132.3) * mm});
            skLineSegment(sketch, "E82.4.1", {"start": v(15, 68.37) * mm, "end": v(15, 132.3) * mm});
            skArc(sketch, "E82.4.2", {"start": v(15, 132.3) * mm, "mid": v(30.9, 140.7) * mm, "end": v(42.8, 154.17) * mm});
            skCircle(sketch, "E82.4.3", {"center": v(0, 180) * mm, "radius": 20 * mm});
            skArc(sketch, "E82.4.4", {"start": v(49.89, 183.33) * mm, "mid": v(39.3, 210.9) * mm, "end": v(15, 227.7) * mm});
            skArc(sketch, "E82.4.5", {"start": v(-15, 227.7) * mm, "mid": v(-39.3, 210.9) * mm, "end": v(-49.89, 183.33) * mm});
            skArc(sketch, "E82.4.6", {"start": v(-42.8, 154.17) * mm, "mid": v(-30.9, 140.7) * mm, "end": v(-15, 132.3) * mm});
            skLineSegment(sketch, "E82.4.7", {"start": v(-15, 227.7) * mm, "end": v(-15, 279.6) * mm});
            skLineSegment(sketch, "E82.4.8", {"start": v(15, 227.7) * mm, "end": v(15, 279.6) * mm});
            skLineSegment(sketch, "E82.5.0", {"start": v(-58.95, 37.74) * mm, "end": v(-104.16, 82.95) * mm});
            skLineSegment(sketch, "E82.5.1", {"start": v(-37.74, 58.95) * mm, "end": v(-82.95, 104.16) * mm});
            skArc(sketch, "E82.5.2", {"start": v(-82.95, 104.16) * mm, "mid": v(-77.63, 121.34) * mm, "end": v(-78.74, 139.28) * mm});
            skCircle(sketch, "E82.5.3", {"center": v(-127.28, 127.28) * mm, "radius": 20 * mm});
            skArc(sketch, "E82.5.4", {"start": v(-94.36, 164.91) * mm, "mid": v(-121.34, 176.93) * mm, "end": v(-150.4, 171.61) * mm});
            skArc(sketch, "E82.5.5", {"start": v(-171.61, 150.4) * mm, "mid": v(-176.93, 121.34) * mm, "end": v(-164.91, 94.36) * mm});
            skArc(sketch, "E82.5.6", {"start": v(-139.28, 78.74) * mm, "mid": v(-121.34, 77.63) * mm, "end": v(-104.16, 82.95) * mm});
            skLineSegment(sketch, "E82.5.7", {"start": v(-171.61, 150.4) * mm, "end": v(-208.31, 187.1) * mm});
            skLineSegment(sketch, "E82.5.8", {"start": v(-150.4, 171.61) * mm, "end": v(-187.1, 208.31) * mm});
            skLineSegment(sketch, "E82.6.0", {"start": v(-68.37, -15) * mm, "end": v(-132.3, -15) * mm});
            skLineSegment(sketch, "E82.6.1", {"start": v(-68.37, 15) * mm, "end": v(-132.3, 15) * mm});
            skArc(sketch, "E82.6.2", {"start": v(-132.3, 15) * mm, "mid": v(-140.7, 30.9) * mm, "end": v(-154.17, 42.8) * mm});
            skCircle(sketch, "E82.6.3", {"center": v(-180, 0) * mm, "radius": 20 * mm});
            skArc(sketch, "E82.6.4", {"start": v(-183.33, 49.89) * mm, "mid": v(-210.9, 39.3) * mm, "end": v(-227.7, 15) * mm});
            skArc(sketch, "E82.6.5", {"start": v(-227.7, -15) * mm, "mid": v(-210.9, -39.3) * mm, "end": v(-183.33, -49.89) * mm});
            skArc(sketch, "E82.6.6", {"start": v(-154.17, -42.8) * mm, "mid": v(-140.7, -30.9) * mm, "end": v(-132.3, -15) * mm});
            skLineSegment(sketch, "E82.6.7", {"start": v(-227.7, -15) * mm, "end": v(-279.6, -15) * mm});
            skLineSegment(sketch, "E82.6.8", {"start": v(-227.7, 15) * mm, "end": v(-279.6, 15) * mm});
            skLineSegment(sketch, "E82.7.0", {"start": v(-37.74, -58.95) * mm, "end": v(-82.95, -104.16) * mm});
            skLineSegment(sketch, "E82.7.1", {"start": v(-58.95, -37.74) * mm, "end": v(-104.16, -82.95) * mm});
            skArc(sketch, "E82.7.2", {"start": v(-104.16, -82.95) * mm, "mid": v(-121.34, -77.63) * mm, "end": v(-139.28, -78.74) * mm});
            skCircle(sketch, "E82.7.3", {"center": v(-127.28, -127.28) * mm, "radius": 20 * mm});
            skArc(sketch, "E82.7.4", {"start": v(-164.91, -94.36) * mm, "mid": v(-176.93, -121.34) * mm, "end": v(-171.61, -150.4) * mm});
            skArc(sketch, "E82.7.5", {"start": v(-150.4, -171.61) * mm, "mid": v(-121.34, -176.93) * mm, "end": v(-94.36, -164.91) * mm});
            skArc(sketch, "E82.7.6", {"start": v(-78.74, -139.28) * mm, "mid": v(-77.63, -121.34) * mm, "end": v(-82.95, -104.16) * mm});
            skLineSegment(sketch, "E82.7.7", {"start": v(-150.4, -171.61) * mm, "end": v(-187.1, -208.31) * mm});
            skLineSegment(sketch, "E82.7.8", {"start": v(-171.61, -150.4) * mm, "end": v(-208.31, -187.1) * mm});
            skArc(sketch, "E83.trimOffspring", {"start": v(-94.36, -164.91) * mm, "mid": v(-72.7, -175.54) * mm, "end": v(-49.89, -183.33) * mm});
            skArc(sketch, "E84.trimOffspring", {"start": v(-78.74, -139.28) * mm, "mid": v(-61.23, -147.82) * mm, "end": v(-42.8, -154.17) * mm});
            skArc(sketch, "E85.trimOffspring", {"start": v(-187.1, -208.31) * mm, "mid": v(-107.15, -258.69) * mm, "end": v(-15, -279.6) * mm});
            skArc(sketch, "E86.trimOffspring", {"start": v(-37.74, -58.95) * mm, "mid": v(-26.79, -64.67) * mm, "end": v(-15, -68.37) * mm});
            skArc(sketch, "E87.trimOffspring", {"start": v(-68.37, -15) * mm, "mid": v(-64.67, -26.79) * mm, "end": v(-58.95, -37.74) * mm});
            skArc(sketch, "E88.trimOffspring", {"start": v(-154.17, -42.8) * mm, "mid": v(-147.82, -61.23) * mm, "end": v(-139.28, -78.74) * mm});
            skArc(sketch, "E89.trimOffspring", {"start": v(-183.33, -49.89) * mm, "mid": v(-175.54, -72.7) * mm, "end": v(-164.91, -94.36) * mm});
            skArc(sketch, "E90.trimOffspring", {"start": v(-279.6, -15) * mm, "mid": v(-258.69, -107.15) * mm, "end": v(-208.31, -187.1) * mm});
            skArc(sketch, "E91.trimOffspring", {"start": v(-164.91, 94.36) * mm, "mid": v(-175.54, 72.7) * mm, "end": v(-183.33, 49.89) * mm});
            skArc(sketch, "E92.trimOffspring", {"start": v(-139.28, 78.74) * mm, "mid": v(-147.82, 61.23) * mm, "end": v(-154.17, 42.8) * mm});
            skArc(sketch, "E93.trimOffspring", {"start": v(-208.31, 187.1) * mm, "mid": v(-258.69, 107.15) * mm, "end": v(-279.6, 15) * mm});
            skArc(sketch, "E94.trimOffspring", {"start": v(-58.95, 37.74) * mm, "mid": v(-64.67, 26.79) * mm, "end": v(-68.37, 15) * mm});
            skArc(sketch, "E95.trimOffspring", {"start": v(-15, 68.37) * mm, "mid": v(-26.79, 64.67) * mm, "end": v(-37.74, 58.95) * mm});
            skArc(sketch, "E96.trimOffspring", {"start": v(-42.8, 154.17) * mm, "mid": v(-61.23, 147.82) * mm, "end": v(-78.74, 139.28) * mm});
            skArc(sketch, "E97.trimOffspring", {"start": v(-49.89, 183.33) * mm, "mid": v(-72.7, 175.54) * mm, "end": v(-94.36, 164.91) * mm});
            skArc(sketch, "E98.trimOffspring", {"start": v(78.74, 139.28) * mm, "mid": v(61.23, 147.82) * mm, "end": v(42.8, 154.17) * mm});
            skArc(sketch, "E99.trimOffspring", {"start": v(94.36, 164.91) * mm, "mid": v(72.7, 175.54) * mm, "end": v(49.89, 183.33) * mm});
            skArc(sketch, "E100.trimOffspring", {"start": v(183.33, 49.89) * mm, "mid": v(175.54, 72.7) * mm, "end": v(164.91, 94.36) * mm});
            skArc(sketch, "E101.trimOffspring", {"start": v(154.17, 42.8) * mm, "mid": v(147.82, 61.23) * mm, "end": v(139.28, 78.74) * mm});
            skArc(sketch, "E102.trimOffspring", {"start": v(68.37, 15) * mm, "mid": v(64.67, 26.79) * mm, "end": v(58.95, 37.74) * mm});
            skArc(sketch, "E103.trimOffspring", {"start": v(279.6, 15) * mm, "mid": v(258.69, 107.15) * mm, "end": v(208.31, 187.1) * mm});
            skArc(sketch, "E104.trimOffspring", {"start": v(58.95, -37.74) * mm, "mid": v(64.67, -26.79) * mm, "end": v(68.37, -15) * mm});
            skArc(sketch, "E105.trimOffspring", {"start": v(139.28, -78.74) * mm, "mid": v(147.82, -61.23) * mm, "end": v(154.17, -42.8) * mm});
            skArc(sketch, "E106.trimOffspring", {"start": v(164.91, -94.36) * mm, "mid": v(175.54, -72.7) * mm, "end": v(183.33, -49.89) * mm});
            skArc(sketch, "E107.trimOffspring", {"start": v(208.31, -187.1) * mm, "mid": v(258.69, -107.15) * mm, "end": v(279.6, -15) * mm});
            skArc(sketch, "E108.trimOffspring", {"start": v(37.74, 58.95) * mm, "mid": v(26.79, 64.67) * mm, "end": v(15, 68.37) * mm});
            skLineSegment(sketch, "E109.0", {"start": v(-4.9, 290) * mm, "end": v(-4.9, 300) * mm});
            skLineSegment(sketch, "E110.0", {"start": v(-1, 300) * mm, "end": v(-4.9, 300) * mm});
            skLineSegment(sketch, "E111.0", {"start": v(0, 301) * mm, "end": v(-1, 300) * mm});
            skLineSegment(sketch, "E112.0", {"start": v(0, 301) * mm, "end": v(1, 300) * mm});
            skLineSegment(sketch, "E113.0", {"start": v(4.9, 300) * mm, "end": v(1, 300) * mm});
            skLineSegment(sketch, "E114.0", {"start": v(4.9, 290) * mm, "end": v(4.9, 300) * mm});
            skLineSegment(sketch, "E115.0", {"start": v(-1, 290) * mm, "end": v(-4.9, 290) * mm});
            skLineSegment(sketch, "E116.0", {"start": v(0, 289) * mm, "end": v(-1, 290) * mm});
            skLineSegment(sketch, "E117.0", {"start": v(0, 289) * mm, "end": v(1, 290) * mm});
            skLineSegment(sketch, "E118.0", {"start": v(4.9, 290) * mm, "end": v(1, 290) * mm});
            skArc(sketch, "E119.trimOffspring", {"start": v(-15, 279.6) * mm, "mid": v(-107.15, 258.69) * mm, "end": v(-187.1, 208.31) * mm});
            skArc(sketch, "E120.trimOffspring", {"start": v(187.1, 208.31) * mm, "mid": v(107.15, 258.69) * mm, "end": v(15, 279.6) * mm});
            skLineSegment(sketch, "E121.1.0", {"start": v(-205.77, 204.35) * mm, "end": v(-208.53, 201.6) * mm});
            skLineSegment(sketch, "E121.1.1", {"start": v(-208.67, 215.6) * mm, "end": v(-211.42, 212.84) * mm});
            skLineSegment(sketch, "E121.1.2", {"start": v(-201.6, 208.53) * mm, "end": v(-204.35, 205.77) * mm});
            skLineSegment(sketch, "E121.1.3", {"start": v(-212.84, 211.42) * mm, "end": v(-215.6, 208.67) * mm});
            skLineSegment(sketch, "E121.1.4", {"start": v(-208.53, 201.6) * mm, "end": v(-215.6, 208.67) * mm});
            skLineSegment(sketch, "E121.1.5", {"start": v(-201.6, 208.53) * mm, "end": v(-208.67, 215.6) * mm});
            skLineSegment(sketch, "E121.1.6", {"start": v(-212.84, 212.84) * mm, "end": v(-211.42, 212.84) * mm});
            skLineSegment(sketch, "E121.1.7", {"start": v(-204.35, 204.35) * mm, "end": v(-204.35, 205.77) * mm});
            skLineSegment(sketch, "E121.1.8", {"start": v(-204.35, 204.35) * mm, "end": v(-205.77, 204.35) * mm});
            skLineSegment(sketch, "E121.1.9", {"start": v(-212.84, 212.84) * mm, "end": v(-212.84, 211.42) * mm});
            skLineSegment(sketch, "E121.2.0", {"start": v(-290, -1) * mm, "end": v(-290, -4.9) * mm});
            skLineSegment(sketch, "E121.2.1", {"start": v(-300, 4.9) * mm, "end": v(-300, 1) * mm});
            skLineSegment(sketch, "E121.2.2", {"start": v(-290, 4.9) * mm, "end": v(-290, 1) * mm});
            skLineSegment(sketch, "E121.2.3", {"start": v(-300, -1) * mm, "end": v(-300, -4.9) * mm});
            skLineSegment(sketch, "E121.2.4", {"start": v(-290, -4.9) * mm, "end": v(-300, -4.9) * mm});
            skLineSegment(sketch, "E121.2.5", {"start": v(-290, 4.9) * mm, "end": v(-300, 4.9) * mm});
            skLineSegment(sketch, "E121.2.6", {"start": v(-301, 0) * mm, "end": v(-300, 1) * mm});
            skLineSegment(sketch, "E121.2.7", {"start": v(-289, 0) * mm, "end": v(-290, 1) * mm});
            skLineSegment(sketch, "E121.2.8", {"start": v(-289, 0) * mm, "end": v(-290, -1) * mm});
            skLineSegment(sketch, "E121.2.9", {"start": v(-301, 0) * mm, "end": v(-300, -1) * mm});
            skLineSegment(sketch, "E121.3.0", {"start": v(-204.35, -205.77) * mm, "end": v(-201.6, -208.53) * mm});
            skLineSegment(sketch, "E121.3.1", {"start": v(-215.6, -208.67) * mm, "end": v(-212.84, -211.42) * mm});
            skLineSegment(sketch, "E121.3.2", {"start": v(-208.53, -201.6) * mm, "end": v(-205.77, -204.35) * mm});
            skLineSegment(sketch, "E121.3.3", {"start": v(-211.42, -212.84) * mm, "end": v(-208.67, -215.6) * mm});
            skLineSegment(sketch, "E121.3.4", {"start": v(-201.6, -208.53) * mm, "end": v(-208.67, -215.6) * mm});
            skLineSegment(sketch, "E121.3.5", {"start": v(-208.53, -201.6) * mm, "end": v(-215.6, -208.67) * mm});
            skLineSegment(sketch, "E121.3.6", {"start": v(-212.84, -212.84) * mm, "end": v(-212.84, -211.42) * mm});
            skLineSegment(sketch, "E121.3.7", {"start": v(-204.35, -204.35) * mm, "end": v(-205.77, -204.35) * mm});
            skLineSegment(sketch, "E121.3.8", {"start": v(-204.35, -204.35) * mm, "end": v(-204.35, -205.77) * mm});
            skLineSegment(sketch, "E121.3.9", {"start": v(-212.84, -212.84) * mm, "end": v(-211.42, -212.84) * mm});
            skLineSegment(sketch, "E121.4.0", {"start": v(1, -290) * mm, "end": v(4.9, -290) * mm});
            skLineSegment(sketch, "E121.4.1", {"start": v(-4.9, -300) * mm, "end": v(-1, -300) * mm});
            skLineSegment(sketch, "E121.4.2", {"start": v(-4.9, -290) * mm, "end": v(-1, -290) * mm});
            skLineSegment(sketch, "E121.4.3", {"start": v(1, -300) * mm, "end": v(4.9, -300) * mm});
            skLineSegment(sketch, "E121.4.4", {"start": v(4.9, -290) * mm, "end": v(4.9, -300) * mm});
            skLineSegment(sketch, "E121.4.5", {"start": v(-4.9, -290) * mm, "end": v(-4.9, -300) * mm});
            skLineSegment(sketch, "E121.4.6", {"start": v(0, -301) * mm, "end": v(-1, -300) * mm});
            skLineSegment(sketch, "E121.4.7", {"start": v(0, -289) * mm, "end": v(-1, -290) * mm});
            skLineSegment(sketch, "E121.4.8", {"start": v(0, -289) * mm, "end": v(1, -290) * mm});
            skLineSegment(sketch, "E121.4.9", {"start": v(0, -301) * mm, "end": v(1, -300) * mm});
            skLineSegment(sketch, "E121.5.0", {"start": v(205.77, -204.35) * mm, "end": v(208.53, -201.6) * mm});
            skLineSegment(sketch, "E121.5.1", {"start": v(208.67, -215.6) * mm, "end": v(211.42, -212.84) * mm});
            skLineSegment(sketch, "E121.5.2", {"start": v(201.6, -208.53) * mm, "end": v(204.35, -205.77) * mm});
            skLineSegment(sketch, "E121.5.3", {"start": v(212.84, -211.42) * mm, "end": v(215.6, -208.67) * mm});
            skLineSegment(sketch, "E121.5.4", {"start": v(208.53, -201.6) * mm, "end": v(215.6, -208.67) * mm});
            skLineSegment(sketch, "E121.5.5", {"start": v(201.6, -208.53) * mm, "end": v(208.67, -215.6) * mm});
            skLineSegment(sketch, "E121.5.6", {"start": v(212.84, -212.84) * mm, "end": v(211.42, -212.84) * mm});
            skLineSegment(sketch, "E121.5.7", {"start": v(204.35, -204.35) * mm, "end": v(204.35, -205.77) * mm});
            skLineSegment(sketch, "E121.5.8", {"start": v(204.35, -204.35) * mm, "end": v(205.77, -204.35) * mm});
            skLineSegment(sketch, "E121.5.9", {"start": v(212.84, -212.84) * mm, "end": v(212.84, -211.42) * mm});
            skLineSegment(sketch, "E121.6.0", {"start": v(290, 1) * mm, "end": v(290, 4.9) * mm});
            skLineSegment(sketch, "E121.6.1", {"start": v(300, -4.9) * mm, "end": v(300, -1) * mm});
            skLineSegment(sketch, "E121.6.2", {"start": v(290, -4.9) * mm, "end": v(290, -1) * mm});
            skLineSegment(sketch, "E121.6.3", {"start": v(300, 1) * mm, "end": v(300, 4.9) * mm});
            skLineSegment(sketch, "E121.6.4", {"start": v(290, 4.9) * mm, "end": v(300, 4.9) * mm});
            skLineSegment(sketch, "E121.6.5", {"start": v(290, -4.9) * mm, "end": v(300, -4.9) * mm});
            skLineSegment(sketch, "E121.6.6", {"start": v(301, 0) * mm, "end": v(300, -1) * mm});
            skLineSegment(sketch, "E121.6.7", {"start": v(289, 0) * mm, "end": v(290, -1) * mm});
            skLineSegment(sketch, "E121.6.8", {"start": v(289, 0) * mm, "end": v(290, 1) * mm});
            skLineSegment(sketch, "E121.6.9", {"start": v(301, 0) * mm, "end": v(300, 1) * mm});
            skLineSegment(sketch, "E121.7.0", {"start": v(204.35, 205.77) * mm, "end": v(201.6, 208.53) * mm});
            skLineSegment(sketch, "E121.7.1", {"start": v(215.6, 208.67) * mm, "end": v(212.84, 211.42) * mm});
            skLineSegment(sketch, "E121.7.2", {"start": v(208.53, 201.6) * mm, "end": v(205.77, 204.35) * mm});
            skLineSegment(sketch, "E121.7.3", {"start": v(211.42, 212.84) * mm, "end": v(208.67, 215.6) * mm});
            skLineSegment(sketch, "E121.7.4", {"start": v(201.6, 208.53) * mm, "end": v(208.67, 215.6) * mm});
            skLineSegment(sketch, "E121.7.5", {"start": v(208.53, 201.6) * mm, "end": v(215.6, 208.67) * mm});
            skLineSegment(sketch, "E121.7.6", {"start": v(212.84, 212.84) * mm, "end": v(212.84, 211.42) * mm});
            skLineSegment(sketch, "E121.7.7", {"start": v(204.35, 204.35) * mm, "end": v(205.77, 204.35) * mm});
            skLineSegment(sketch, "E121.7.8", {"start": v(204.35, 204.35) * mm, "end": v(204.35, 205.77) * mm});
            skLineSegment(sketch, "E121.7.9", {"start": v(212.84, 212.84) * mm, "end": v(211.42, 212.84) * mm});
            skSolve(sketch);
        }
        {
            var Q0;
            Q0=qSketchRegion(id+"F6",true);
            extrude(context, id + "F7", {"entities" : qUnion([Q0]), "depth" : 10 * mm, "offsetDistance" : 25 * mm});
        }
        {
            var Q0;
            Q0=qCreatedBy(id+"F1.planeOp",FACE);
            var sketch = newSketch(context, id + "F8", { "sketchPlane" : qUnion([Q0])});
            skCircle(sketch, "E122", {"center": v(0, 0) * mm, "radius": 575 * mm});
            skLineSegment(sketch, "E123.bottom", {"start": v(4.9, 530) * mm, "end": v(1, 530) * mm});
            skLineSegment(sketch, "E123.top", {"start": v(4.9, 540) * mm, "end": v(1, 540) * mm});
            skLineSegment(sketch, "E123.left", {"start": v(4.9, 530) * mm, "end": v(4.9, 540) * mm});
            skLineSegment(sketch, "E123.right", {"start": v(-4.9, 530) * mm, "end": v(-4.9, 540) * mm});
            skPoint(sketch, "E123.middle", {"position": v(0, 535) * mm});
            skLineSegment(sketch, "E124", {"start": v(0, 541) * mm, "end": v(-1, 540) * mm});
            skLineSegment(sketch, "E125", {"start": v(0, 541) * mm, "end": v(1, 540) * mm});
            skLineSegment(sketch, "E126.trimOffspring", {"start": v(-1, 540) * mm, "end": v(-4.9, 540) * mm});
            skLineSegment(sketch, "E127", {"start": v(0, 529) * mm, "end": v(-1, 530) * mm});
            skLineSegment(sketch, "E128", {"start": v(0, 529) * mm, "end": v(1, 530) * mm});
            skLineSegment(sketch, "E129.trimOffspring", {"start": v(-1, 530) * mm, "end": v(-4.9, 530) * mm});
            skPoint(sketch, "E130.2.0", {"position": v(-378.3, 378.3) * mm});
            skLineSegment(sketch, "E130.2.1", {"start": v(-378.23, 371.3) * mm, "end": v(-385.3, 378.37) * mm});
            skLineSegment(sketch, "E130.2.2", {"start": v(-371.3, 378.23) * mm, "end": v(-378.37, 385.3) * mm});
            skLineSegment(sketch, "E130.2.3", {"start": v(-371.3, 378.23) * mm, "end": v(-374.06, 375.47) * mm});
            skLineSegment(sketch, "E130.2.4", {"start": v(-374.06, 374.06) * mm, "end": v(-374.06, 375.47) * mm});
            skLineSegment(sketch, "E130.2.5", {"start": v(-374.06, 374.06) * mm, "end": v(-375.47, 374.06) * mm});
            skLineSegment(sketch, "E130.2.6", {"start": v(-375.47, 374.06) * mm, "end": v(-378.23, 371.3) * mm});
            skLineSegment(sketch, "E130.2.7", {"start": v(-378.37, 385.3) * mm, "end": v(-381.13, 382.54) * mm});
            skLineSegment(sketch, "E130.2.8", {"start": v(-382.54, 381.13) * mm, "end": v(-385.3, 378.37) * mm});
            skLineSegment(sketch, "E130.2.9", {"start": v(-382.54, 382.54) * mm, "end": v(-381.13, 382.54) * mm});
            skLineSegment(sketch, "E130.2.10", {"start": v(-382.54, 382.54) * mm, "end": v(-382.54, 381.13) * mm});
            skPoint(sketch, "E130.4.0", {"position": v(-535, 0) * mm});
            skLineSegment(sketch, "E130.4.1", {"start": v(-530, -4.9) * mm, "end": v(-540, -4.9) * mm});
            skLineSegment(sketch, "E130.4.2", {"start": v(-530, 4.9) * mm, "end": v(-540, 4.9) * mm});
            skLineSegment(sketch, "E130.4.3", {"start": v(-530, 4.9) * mm, "end": v(-530, 1) * mm});
            skLineSegment(sketch, "E130.4.4", {"start": v(-529, 0) * mm, "end": v(-530, 1) * mm});
            skLineSegment(sketch, "E130.4.5", {"start": v(-529, 0) * mm, "end": v(-530, -1) * mm});
            skLineSegment(sketch, "E130.4.6", {"start": v(-530, -1) * mm, "end": v(-530, -4.9) * mm});
            skLineSegment(sketch, "E130.4.7", {"start": v(-540, 4.9) * mm, "end": v(-540, 1) * mm});
            skLineSegment(sketch, "E130.4.8", {"start": v(-540, -1) * mm, "end": v(-540, -4.9) * mm});
            skLineSegment(sketch, "E130.4.9", {"start": v(-541, 0) * mm, "end": v(-540, 1) * mm});
            skLineSegment(sketch, "E130.4.10", {"start": v(-541, 0) * mm, "end": v(-540, -1) * mm});
            skPoint(sketch, "E130.6.0", {"position": v(-378.3, -378.3) * mm});
            skLineSegment(sketch, "E130.6.1", {"start": v(-371.3, -378.23) * mm, "end": v(-378.37, -385.3) * mm});
            skLineSegment(sketch, "E130.6.2", {"start": v(-378.23, -371.3) * mm, "end": v(-385.3, -378.37) * mm});
            skLineSegment(sketch, "E130.6.3", {"start": v(-378.23, -371.3) * mm, "end": v(-375.47, -374.06) * mm});
            skLineSegment(sketch, "E130.6.4", {"start": v(-374.06, -374.06) * mm, "end": v(-375.47, -374.06) * mm});
            skLineSegment(sketch, "E130.6.5", {"start": v(-374.06, -374.06) * mm, "end": v(-374.06, -375.47) * mm});
            skLineSegment(sketch, "E130.6.6", {"start": v(-374.06, -375.47) * mm, "end": v(-371.3, -378.23) * mm});
            skLineSegment(sketch, "E130.6.7", {"start": v(-385.3, -378.37) * mm, "end": v(-382.54, -381.13) * mm});
            skLineSegment(sketch, "E130.6.8", {"start": v(-381.13, -382.54) * mm, "end": v(-378.37, -385.3) * mm});
            skLineSegment(sketch, "E130.6.9", {"start": v(-382.54, -382.54) * mm, "end": v(-382.54, -381.13) * mm});
            skLineSegment(sketch, "E130.6.10", {"start": v(-382.54, -382.54) * mm, "end": v(-381.13, -382.54) * mm});
            skPoint(sketch, "E130.8.0", {"position": v(0, -535) * mm});
            skLineSegment(sketch, "E130.8.1", {"start": v(4.9, -530) * mm, "end": v(4.9, -540) * mm});
            skLineSegment(sketch, "E130.8.2", {"start": v(-4.9, -530) * mm, "end": v(-4.9, -540) * mm});
            skLineSegment(sketch, "E130.8.3", {"start": v(-4.9, -530) * mm, "end": v(-1, -530) * mm});
            skLineSegment(sketch, "E130.8.4", {"start": v(0, -529) * mm, "end": v(-1, -530) * mm});
            skLineSegment(sketch, "E130.8.5", {"start": v(0, -529) * mm, "end": v(1, -530) * mm});
            skLineSegment(sketch, "E130.8.6", {"start": v(1, -530) * mm, "end": v(4.9, -530) * mm});
            skLineSegment(sketch, "E130.8.7", {"start": v(-4.9, -540) * mm, "end": v(-1, -540) * mm});
            skLineSegment(sketch, "E130.8.8", {"start": v(1, -540) * mm, "end": v(4.9, -540) * mm});
            skLineSegment(sketch, "E130.8.9", {"start": v(0, -541) * mm, "end": v(-1, -540) * mm});
            skLineSegment(sketch, "E130.8.10", {"start": v(0, -541) * mm, "end": v(1, -540) * mm});
            skPoint(sketch, "E130.10.0", {"position": v(378.3, -378.3) * mm});
            skLineSegment(sketch, "E130.10.1", {"start": v(378.23, -371.3) * mm, "end": v(385.3, -378.37) * mm});
            skLineSegment(sketch, "E130.10.2", {"start": v(371.3, -378.23) * mm, "end": v(378.37, -385.3) * mm});
            skLineSegment(sketch, "E130.10.3", {"start": v(371.3, -378.23) * mm, "end": v(374.06, -375.47) * mm});
            skLineSegment(sketch, "E130.10.4", {"start": v(374.06, -374.06) * mm, "end": v(374.06, -375.47) * mm});
            skLineSegment(sketch, "E130.10.5", {"start": v(374.06, -374.06) * mm, "end": v(375.47, -374.06) * mm});
            skLineSegment(sketch, "E130.10.6", {"start": v(375.47, -374.06) * mm, "end": v(378.23, -371.3) * mm});
            skLineSegment(sketch, "E130.10.7", {"start": v(378.37, -385.3) * mm, "end": v(381.13, -382.54) * mm});
            skLineSegment(sketch, "E130.10.8", {"start": v(382.54, -381.13) * mm, "end": v(385.3, -378.37) * mm});
            skLineSegment(sketch, "E130.10.9", {"start": v(382.54, -382.54) * mm, "end": v(381.13, -382.54) * mm});
            skLineSegment(sketch, "E130.10.10", {"start": v(382.54, -382.54) * mm, "end": v(382.54, -381.13) * mm});
            skPoint(sketch, "E130.12.0", {"position": v(535, 0) * mm});
            skLineSegment(sketch, "E130.12.1", {"start": v(530, 4.9) * mm, "end": v(540, 4.9) * mm});
            skLineSegment(sketch, "E130.12.2", {"start": v(530, -4.9) * mm, "end": v(540, -4.9) * mm});
            skLineSegment(sketch, "E130.12.3", {"start": v(530, -4.9) * mm, "end": v(530, -1) * mm});
            skLineSegment(sketch, "E130.12.4", {"start": v(529, 0) * mm, "end": v(530, -1) * mm});
            skLineSegment(sketch, "E130.12.5", {"start": v(529, 0) * mm, "end": v(530, 1) * mm});
            skLineSegment(sketch, "E130.12.6", {"start": v(530, 1) * mm, "end": v(530, 4.9) * mm});
            skLineSegment(sketch, "E130.12.7", {"start": v(540, -4.9) * mm, "end": v(540, -1) * mm});
            skLineSegment(sketch, "E130.12.8", {"start": v(540, 1) * mm, "end": v(540, 4.9) * mm});
            skLineSegment(sketch, "E130.12.9", {"start": v(541, 0) * mm, "end": v(540, -1) * mm});
            skLineSegment(sketch, "E130.12.10", {"start": v(541, 0) * mm, "end": v(540, 1) * mm});
            skPoint(sketch, "E130.14.0", {"position": v(378.3, 378.3) * mm});
            skLineSegment(sketch, "E130.14.1", {"start": v(371.3, 378.23) * mm, "end": v(378.37, 385.3) * mm});
            skLineSegment(sketch, "E130.14.2", {"start": v(378.23, 371.3) * mm, "end": v(385.3, 378.37) * mm});
            skLineSegment(sketch, "E130.14.3", {"start": v(378.23, 371.3) * mm, "end": v(375.47, 374.06) * mm});
            skLineSegment(sketch, "E130.14.4", {"start": v(374.06, 374.06) * mm, "end": v(375.47, 374.06) * mm});
            skLineSegment(sketch, "E130.14.5", {"start": v(374.06, 374.06) * mm, "end": v(374.06, 375.47) * mm});
            skLineSegment(sketch, "E130.14.6", {"start": v(374.06, 375.47) * mm, "end": v(371.3, 378.23) * mm});
            skLineSegment(sketch, "E130.14.7", {"start": v(385.3, 378.37) * mm, "end": v(382.54, 381.13) * mm});
            skLineSegment(sketch, "E130.14.8", {"start": v(381.13, 382.54) * mm, "end": v(378.37, 385.3) * mm});
            skLineSegment(sketch, "E130.14.9", {"start": v(382.54, 382.54) * mm, "end": v(382.54, 381.13) * mm});
            skLineSegment(sketch, "E130.14.10", {"start": v(382.54, 382.54) * mm, "end": v(381.13, 382.54) * mm});
            skCircle(sketch, "E131", {"center": v(0, 0) * mm, "radius": 500 * mm});
            skSolve(sketch);
        }
        {
            var Q0;
            Q0=qSketchRegion(id+"F8",true);
            extrude(context, id + "F9", {"entities" : qUnion([Q0]), "depth" : 10 * mm, "offsetDistance" : 25 * mm});
        }
        {
            var Q0;
            Q0=qCreatedBy(makeId("Right.planeOp"),FACE);
            var sketch = newSketch(context, id + "F10", { "sketchPlane" : qUnion([Q0])});
            skLineSegment(sketch, "E132.0.1", {"start": v(540, 0) * mm, "end": v(540, 10) * mm});
            skLineSegment(sketch, "E132.0.2", {"start": v(540, 10) * mm, "end": v(530, 10) * mm});
            skLineSegment(sketch, "E132.0.3", {"start": v(530, 10) * mm, "end": v(530, 0) * mm});
            skLineSegment(sketch, "E133.0.0", {"start": v(530, -200) * mm, "end": v(540, -200) * mm});
            skLineSegment(sketch, "E133.0.1", {"start": v(540, -200) * mm, "end": v(540, -190) * mm});
            skLineSegment(sketch, "E133.0.3", {"start": v(530, -190) * mm, "end": v(530, -200) * mm});
            skLineSegment(sketch, "E134", {"start": v(530, 0) * mm, "end": v(520, 0) * mm});
            skLineSegment(sketch, "E135", {"start": v(520, 0) * mm, "end": v(520, -90.1) * mm});
            skLineSegment(sketch, "E136", {"start": v(520, -190) * mm, "end": v(530, -190) * mm});
            skLineSegment(sketch, "E137", {"start": v(540, -190) * mm, "end": v(550, -190) * mm});
            skLineSegment(sketch, "E138", {"start": v(550, -190) * mm, "end": v(550, 0) * mm});
            skLineSegment(sketch, "E139", {"start": v(550, 0) * mm, "end": v(540, 0) * mm});
            skLineSegment(sketch, "E140.0.0", {"start": v(290, 0) * mm, "end": v(300, 0) * mm});
            skLineSegment(sketch, "E140.0.1", {"start": v(300, 0) * mm, "end": v(300, 10) * mm});
            skLineSegment(sketch, "E140.0.3", {"start": v(290, 10) * mm, "end": v(290, 0) * mm});
            skLineSegment(sketch, "E141.0.1", {"start": v(300, 200) * mm, "end": v(300, 210) * mm});
            skLineSegment(sketch, "E141.0.2", {"start": v(300, 210) * mm, "end": v(290, 210) * mm});
            skLineSegment(sketch, "E141.0.3", {"start": v(290, 210) * mm, "end": v(290, 200) * mm});
            skLineSegment(sketch, "E142", {"start": v(290, 200) * mm, "end": v(280, 200) * mm});
            skLineSegment(sketch, "E143", {"start": v(280, 200) * mm, "end": v(280, 109.9) * mm});
            skLineSegment(sketch, "E144", {"start": v(280, 10) * mm, "end": v(290, 10) * mm});
            skLineSegment(sketch, "E145", {"start": v(300, 10) * mm, "end": v(310, 10) * mm});
            skLineSegment(sketch, "E146", {"start": v(310, 10) * mm, "end": v(310, 200) * mm});
            skLineSegment(sketch, "E147", {"start": v(310, 200) * mm, "end": v(300, 200) * mm});
            skLineSegment(sketch, "E148", {"start": v(280, 109.9) * mm, "end": v(290, 109.9) * mm});
            skLineSegment(sketch, "E149", {"start": v(290, 109.9) * mm, "end": v(290, 100.1) * mm});
            skLineSegment(sketch, "E150", {"start": v(290, 100.1) * mm, "end": v(280, 100.1) * mm});
            skLineSegment(sketch, "E151.trimOffspring", {"start": v(280, 100.1) * mm, "end": v(280, 10) * mm});
            skLineSegment(sketch, "E152", {"start": v(520, -90.1) * mm, "end": v(530, -90.1) * mm});
            skLineSegment(sketch, "E153", {"start": v(530, -90.1) * mm, "end": v(530, -99.9) * mm});
            skLineSegment(sketch, "E154", {"start": v(530, -99.9) * mm, "end": v(520, -99.9) * mm});
            skLineSegment(sketch, "E155.trimOffspring", {"start": v(520, -99.9) * mm, "end": v(520, -190) * mm});
            skSolve(sketch);
        }
        {
            var Q0;
            Q0 = qSketchRegion(id + "F10", true);
            extrude(context, id + "F11", {"entities" : qUnion([Q0]), "endBound" : BoundingType.SYMMETRIC, "depth" : 10 * mm, "offsetDistance" : 25 * mm});
        }
        {
            var Q0;
            Q0=makeQuery(id+"F11.opExtrude","SWEPT_BODY",BODY,{"disambiguationData":[OSD([sQuery(id+"F10.wireOp",EDGE,"E132.0.1"),sQuery(id+"F10.wireOp",EDGE,"E132.0.2"),sQuery(id+"F10.wireOp",EDGE,"E132.0.3"),sQuery(id+"F10.wireOp",EDGE,"E133.0.0"),sQuery(id+"F10.wireOp",EDGE,"E133.0.1"),sQuery(id+"F10.wireOp",EDGE,"E133.0.3"),sQuery(id+"F10.wireOp",EDGE,"E134"),sQuery(id+"F10.wireOp",EDGE,"E135"),sQuery(id+"F10.wireOp",EDGE,"E136"),sQuery(id+"F10.wireOp",EDGE,"E137"),sQuery(id+"F10.wireOp",EDGE,"E138"),sQuery(id+"F10.wireOp",EDGE,"E139")])]});
            var Q1;
            Q1=makeQuery(id+"F11.opExtrude","SWEPT_BODY",BODY,{"disambiguationData":[OSD([sQuery(id+"F10.wireOp",EDGE,"E140.0.0"),sQuery(id+"F10.wireOp",EDGE,"E140.0.1"),sQuery(id+"F10.wireOp",EDGE,"E140.0.3"),sQuery(id+"F10.wireOp",EDGE,"E141.0.1"),sQuery(id+"F10.wireOp",EDGE,"E141.0.2"),sQuery(id+"F10.wireOp",EDGE,"E141.0.3"),sQuery(id+"F10.wireOp",EDGE,"E142"),sQuery(id+"F10.wireOp",EDGE,"E143"),sQuery(id+"F10.wireOp",EDGE,"E144"),sQuery(id+"F10.wireOp",EDGE,"E145"),sQuery(id+"F10.wireOp",EDGE,"E146"),sQuery(id+"F10.wireOp",EDGE,"E147")])]});
            var Q2;
            Q2=makeQuery(id+"F7.opExtrude","CAP_EDGE",EDGE,{"disambiguationData":[OSD([sQuery(id+"F6.wireOp",EDGE,"E70.0")])],"isStart":false});
            circularPattern(context, id + "F12", {"operationType" : NewBodyOperationType.ADD, "entities" : qUnion([Q0, Q1]), "axis" : qUnion([Q2]), "angle" : 360 * degree, "instanceCount" : 8, "equalSpace" : true});
        }
        {
            var Q0;
            Q0=qCreatedBy(id+"F2.planeOp",FACE);
            var sketch = newSketch(context, id + "F13", { "sketchPlane" : qUnion([Q0])});
            skPoint(sketch, "E156.0", {"position": v(-520, 0) * mm});
            skPoint(sketch, "E157.0", {"position": v(-540, 0) * mm});
            skPoint(sketch, "E158.0", {"position": v(-530, -5) * mm});
            skPoint(sketch, "E159.0", {"position": v(-530, 5) * mm});
            skArc(sketch, "E160", {"start": v(-539.98, -5) * mm, "mid": v(-498.9, -206.65) * mm, "end": v(-385.36, -378.29) * mm});
            skCircle(sketch, "E161", {"center": v(0, 0) * mm, "radius": 520 * mm});
            skLineSegment(sketch, "E162", {"start": v(-530, 5) * mm, "end": v(-530, -5) * mm});
            skLineSegment(sketch, "E163", {"start": v(-530, 5) * mm, "end": v(-539.98, 5) * mm});
            skLineSegment(sketch, "E164", {"start": v(-530, -5) * mm, "end": v(-539.98, -5) * mm});
            skLineSegment(sketch, "E165", {"start": v(-540, 0) * mm, "end": v(-520, 0) * mm, "construction": true});
            skLineSegment(sketch, "E166.1.0", {"start": v(-378.3, -371.23) * mm, "end": v(-385.36, -378.29) * mm});
            skLineSegment(sketch, "E166.1.1", {"start": v(-378.3, -371.23) * mm, "end": v(-371.23, -378.3) * mm});
            skLineSegment(sketch, "E166.1.2", {"start": v(-381.84, -381.84) * mm, "end": v(-367.7, -367.7) * mm, "construction": true});
            skLineSegment(sketch, "E166.1.3", {"start": v(-371.23, -378.3) * mm, "end": v(-378.29, -385.36) * mm});
            skLineSegment(sketch, "E166.2.0", {"start": v(-5, -530) * mm, "end": v(-5, -539.98) * mm});
            skLineSegment(sketch, "E166.2.1", {"start": v(-5, -530) * mm, "end": v(5, -530) * mm});
            skLineSegment(sketch, "E166.2.2", {"start": v(0, -540) * mm, "end": v(0, -520) * mm, "construction": true});
            skLineSegment(sketch, "E166.2.3", {"start": v(5, -530) * mm, "end": v(5, -539.98) * mm});
            skLineSegment(sketch, "E166.3.0", {"start": v(371.23, -378.3) * mm, "end": v(378.29, -385.36) * mm});
            skLineSegment(sketch, "E166.3.1", {"start": v(371.23, -378.3) * mm, "end": v(378.3, -371.23) * mm});
            skLineSegment(sketch, "E166.3.2", {"start": v(381.84, -381.84) * mm, "end": v(367.7, -367.7) * mm, "construction": true});
            skLineSegment(sketch, "E166.3.3", {"start": v(378.3, -371.23) * mm, "end": v(385.36, -378.29) * mm});
            skLineSegment(sketch, "E166.4.0", {"start": v(530, -5) * mm, "end": v(539.98, -5) * mm});
            skLineSegment(sketch, "E166.4.1", {"start": v(530, -5) * mm, "end": v(530, 5) * mm});
            skLineSegment(sketch, "E166.4.2", {"start": v(540, 0) * mm, "end": v(520, 0) * mm, "construction": true});
            skLineSegment(sketch, "E166.4.3", {"start": v(530, 5) * mm, "end": v(539.98, 5) * mm});
            skLineSegment(sketch, "E166.5.0", {"start": v(378.3, 371.23) * mm, "end": v(385.36, 378.29) * mm});
            skLineSegment(sketch, "E166.5.1", {"start": v(378.3, 371.23) * mm, "end": v(371.23, 378.3) * mm});
            skLineSegment(sketch, "E166.5.2", {"start": v(381.84, 381.84) * mm, "end": v(367.7, 367.7) * mm, "construction": true});
            skLineSegment(sketch, "E166.5.3", {"start": v(371.23, 378.3) * mm, "end": v(378.29, 385.36) * mm});
            skLineSegment(sketch, "E166.6.0", {"start": v(5, 530) * mm, "end": v(5, 539.98) * mm});
            skLineSegment(sketch, "E166.6.1", {"start": v(5, 530) * mm, "end": v(-5, 530) * mm});
            skLineSegment(sketch, "E166.6.2", {"start": v(0, 540) * mm, "end": v(0, 520) * mm, "construction": true});
            skLineSegment(sketch, "E166.6.3", {"start": v(-5, 530) * mm, "end": v(-5, 539.98) * mm});
            skLineSegment(sketch, "E166.7.0", {"start": v(-371.23, 378.3) * mm, "end": v(-378.29, 385.36) * mm});
            skLineSegment(sketch, "E166.7.1", {"start": v(-371.23, 378.3) * mm, "end": v(-378.3, 371.23) * mm});
            skLineSegment(sketch, "E166.7.2", {"start": v(-381.84, 381.84) * mm, "end": v(-367.7, 367.7) * mm, "construction": true});
            skLineSegment(sketch, "E166.7.3", {"start": v(-378.3, 371.23) * mm, "end": v(-385.36, 378.29) * mm});
            skArc(sketch, "E167.trimOffspring", {"start": v(-385.36, 378.29) * mm, "mid": v(-498.9, 206.65) * mm, "end": v(-539.98, 5) * mm});
            skArc(sketch, "E168.trimOffspring", {"start": v(-5, 539.98) * mm, "mid": v(-206.65, 498.9) * mm, "end": v(-378.29, 385.36) * mm});
            skArc(sketch, "E169.trimOffspring", {"start": v(378.29, 385.36) * mm, "mid": v(206.65, 498.9) * mm, "end": v(5, 539.98) * mm});
            skArc(sketch, "E170.trimOffspring", {"start": v(539.98, 5) * mm, "mid": v(498.9, 206.65) * mm, "end": v(385.36, 378.29) * mm});
            skArc(sketch, "E171.trimOffspring", {"start": v(385.36, -378.29) * mm, "mid": v(498.9, -206.65) * mm, "end": v(539.98, -5) * mm});
            skArc(sketch, "E172.trimOffspring", {"start": v(5, -539.98) * mm, "mid": v(206.65, -498.9) * mm, "end": v(378.29, -385.36) * mm});
            skArc(sketch, "E173.trimOffspring", {"start": v(-378.29, -385.36) * mm, "mid": v(-206.65, -498.9) * mm, "end": v(-5, -539.98) * mm});
            skSolve(sketch);
        }
        {
            var Q0;
            Q0 = qSketchRegion(id + "F13", true);
            extrude(context, id + "F14", {"entities" : qUnion([Q0]), "depth" : 10 * mm, "offsetDistance" : 25 * mm});
        }
        {
            var Q0;
            Q0=qCreatedBy(id+"F3.planeOp",FACE);
            var sketch = newSketch(context, id + "F15", { "sketchPlane" : qUnion([Q0])});
            skPoint(sketch, "E174.0", {"position": v(-280, 0) * mm});
            skPoint(sketch, "E175.0", {"position": v(-290, -5) * mm});
            skPoint(sketch, "E176.0", {"position": v(-290, 5) * mm});
            skPoint(sketch, "E177.0", {"position": v(-300, 0) * mm});
            skArc(sketch, "E178", {"start": v(-299.96, -5) * mm, "mid": v(-277.16, -114.8) * mm, "end": v(-215.64, -208.57) * mm});
            skCircle(sketch, "E179", {"center": v(0, 0) * mm, "radius": 280 * mm});
            skLineSegment(sketch, "E180", {"start": v(-290, 5) * mm, "end": v(-290, -5) * mm});
            skLineSegment(sketch, "E181", {"start": v(-290, -5) * mm, "end": v(-299.96, -5) * mm});
            skLineSegment(sketch, "E182", {"start": v(-290, 5) * mm, "end": v(-299.96, 5) * mm});
            skLineSegment(sketch, "E183.1.0", {"start": v(-208.6, -201.53) * mm, "end": v(-215.64, -208.57) * mm});
            skLineSegment(sketch, "E183.1.1", {"start": v(-208.6, -201.53) * mm, "end": v(-201.53, -208.6) * mm});
            skLineSegment(sketch, "E183.1.2", {"start": v(-201.53, -208.6) * mm, "end": v(-208.57, -215.64) * mm});
            skLineSegment(sketch, "E183.2.0", {"start": v(-5, -290) * mm, "end": v(-5, -299.96) * mm});
            skLineSegment(sketch, "E183.2.1", {"start": v(-5, -290) * mm, "end": v(5, -290) * mm});
            skLineSegment(sketch, "E183.2.2", {"start": v(5, -290) * mm, "end": v(5, -299.96) * mm});
            skLineSegment(sketch, "E183.3.0", {"start": v(201.53, -208.6) * mm, "end": v(208.57, -215.64) * mm});
            skLineSegment(sketch, "E183.3.1", {"start": v(201.53, -208.6) * mm, "end": v(208.6, -201.53) * mm});
            skLineSegment(sketch, "E183.3.2", {"start": v(208.6, -201.53) * mm, "end": v(215.64, -208.57) * mm});
            skLineSegment(sketch, "E183.4.0", {"start": v(290, -5) * mm, "end": v(299.96, -5) * mm});
            skLineSegment(sketch, "E183.4.1", {"start": v(290, -5) * mm, "end": v(290, 5) * mm});
            skLineSegment(sketch, "E183.4.2", {"start": v(290, 5) * mm, "end": v(299.96, 5) * mm});
            skLineSegment(sketch, "E183.5.0", {"start": v(208.6, 201.53) * mm, "end": v(215.64, 208.57) * mm});
            skLineSegment(sketch, "E183.5.1", {"start": v(208.6, 201.53) * mm, "end": v(201.53, 208.6) * mm});
            skLineSegment(sketch, "E183.5.2", {"start": v(201.53, 208.6) * mm, "end": v(208.57, 215.64) * mm});
            skLineSegment(sketch, "E183.6.0", {"start": v(5, 290) * mm, "end": v(5, 299.96) * mm});
            skLineSegment(sketch, "E183.6.1", {"start": v(5, 290) * mm, "end": v(-5, 290) * mm});
            skLineSegment(sketch, "E183.6.2", {"start": v(-5, 290) * mm, "end": v(-5, 299.96) * mm});
            skLineSegment(sketch, "E183.7.0", {"start": v(-201.53, 208.6) * mm, "end": v(-208.57, 215.64) * mm});
            skLineSegment(sketch, "E183.7.1", {"start": v(-201.53, 208.6) * mm, "end": v(-208.6, 201.53) * mm});
            skLineSegment(sketch, "E183.7.2", {"start": v(-208.6, 201.53) * mm, "end": v(-215.64, 208.57) * mm});
            skArc(sketch, "E184.trimOffspring", {"start": v(-215.64, 208.57) * mm, "mid": v(-277.16, 114.8) * mm, "end": v(-299.96, 5) * mm});
            skArc(sketch, "E185.trimOffspring", {"start": v(-5, 299.96) * mm, "mid": v(-114.8, 277.16) * mm, "end": v(-208.57, 215.64) * mm});
            skArc(sketch, "E186.trimOffspring", {"start": v(208.57, 215.64) * mm, "mid": v(114.8, 277.16) * mm, "end": v(5, 299.96) * mm});
            skArc(sketch, "E187.trimOffspring", {"start": v(299.96, 5) * mm, "mid": v(277.16, 114.8) * mm, "end": v(215.64, 208.57) * mm});
            skArc(sketch, "E188.trimOffspring", {"start": v(215.64, -208.57) * mm, "mid": v(277.16, -114.8) * mm, "end": v(299.96, -5) * mm});
            skArc(sketch, "E189.trimOffspring", {"start": v(5, -299.96) * mm, "mid": v(114.8, -277.16) * mm, "end": v(208.57, -215.64) * mm});
            skArc(sketch, "E190.trimOffspring", {"start": v(-208.57, -215.64) * mm, "mid": v(-114.8, -277.16) * mm, "end": v(-5, -299.96) * mm});
            skSolve(sketch);
        }
        {
            var Q0;
            Q0 = qSketchRegion(id + "F15", true);
            extrude(context, id + "F16", {"entities" : qUnion([Q0]), "depth" : 10 * mm, "offsetDistance" : 25 * mm});
        }
    });
